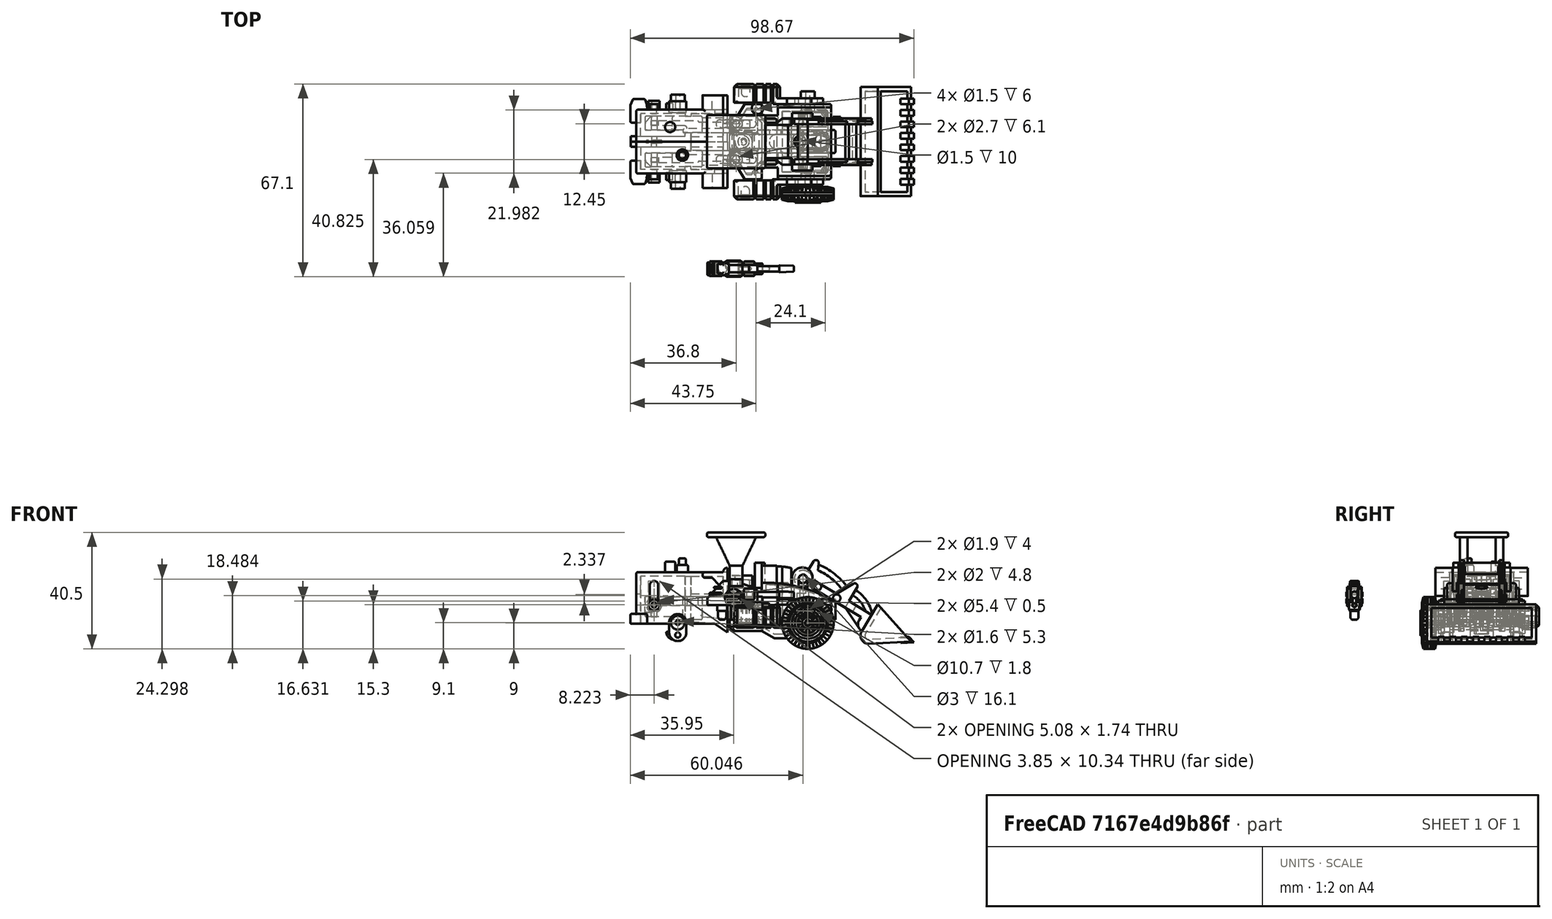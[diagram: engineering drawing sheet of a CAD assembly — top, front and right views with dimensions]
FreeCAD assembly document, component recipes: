
FREECAD ASSEMBLY — COMPONENT RECIPES ("Scrapper")

This assembly document has 14 components, labeled P0..P13 below (a component is one placed body or linked part). 14 of them carry a construction recipe — the FreeCAD feature program that regenerates the part from scratch, quoted from this document or its linked companion documents; the rest are supplied as boundary geometry only. No exploded tour is included for this assembly.
NOTE — document 2 of 4 of this assembly tour. The two overview renders and the header above are repeated from document 1; the component sections below continue where the previous document stopped.
COMPONENT P3 — recipe-attached ("Scoop", modeled in this document).
Construction recipe (the document's own serialized feature program — sketch geometry with constraints, then the solid features built on it; lengths are millimeters unless a unit is written):

FEATURE [Sketcher::SketchObject] Sketch111
  ArcFitTolerance = 1e-06
  AttachmentSupport = -> [XY_Plane004]
  FullyConstrained = true
  MakeInternals = false
  MapMode = 5
  sketch-geometry (4):
    g0: LineSegment StartX=3.75398 StartY=13.5 StartZ=0 EndX=14.5725 EndY=0 EndZ=0
    g1: LineSegment StartX=3.75398 StartY=13.5 StartZ=0 EndX=-2.36 EndY=4.43565 EndZ=0
    g2: ArcOfCircle CenterX=0 CenterY=2.84565 CenterZ=0 NormalX=0 NormalY=0 NormalZ=1 AngleXU=0 Radius=2.84565 StartAngle=2.54872 EndAngle=4.71239
    g3: LineSegment StartX=-5e-16 StartY=0 StartZ=0 EndX=14.5725 EndY=0 EndZ=0
  constraints (12):
    c: PointOnObject(g0,g-1)
    c: Coincident(g1,g0)
    c: Coincident(g2,g1)
    c: Distance(g0) = 17.3
    c: Coincident(g3,g2)
    c: Coincident(g3,g0)
    c: DistanceY(g2,g0) = 13.5
    c: Coincident(g2,g-1)
    c: Angle(g3,g1) = 0.977384
    c: DistanceX(g2,g2) = 0
    c: DistanceX(g1,g2) = 2.36
    c: DistanceY(g2,g1) = 1.59
FEATURE [PartDesign::Pad] Pad065
  Direction = (0,0,1)
  Length = 38
  Length2 = 10
  Profile = -> Sketch111
  ReferenceAxis = -> Sketch111 [N_Axis]
  Refine = true
  Suppressed = false
  Type = 0
FEATURE [Sketcher::SketchObject] Sketch112
  ArcFitTolerance = 1e-06
  AttachmentSupport = -> [Pad065]
  ExternalGeometry = -> [Pad065]
  FullyConstrained = false
  MakeInternals = false
  MapMode = 5
  Placement = pos=(0,0,38) rot=(0,0,1;0rad)
  sketch-geometry (6):
    g0: LineSegment StartX=4.73641 StartY=12.2741 StartZ=0 EndX=-1.11618 EndY=3.59725 EndZ=0
    g1: ArcOfCircle CenterX=0 CenterY=2.84565 CenterZ=0 NormalX=0 NormalY=0 NormalZ=1 AngleXU=0 Radius=1.34565 StartAngle=2.54896 EndAngle=4.71239
    g2: LineSegment StartX=0 StartY=1.5 StartZ=0 EndX=13.3704 EndY=1.5 EndZ=0
    g3: LineSegment [constr] StartX=1.25379 StartY=9.79331 StartZ=0 EndX=2.49735 EndY=8.95452 EndZ=0
    g4: LineSegment [constr] StartX=6.46619 StartY=7.71687 StartZ=0 EndX=7.63671 EndY=8.65489 EndZ=0
    g5: LineSegment StartX=4.73641 StartY=12.2741 StartZ=0 EndX=13.3704 EndY=1.5 EndZ=0
  constraints (19):
    c: Coincident(g1,g0)
    c: PointOnObject(g1,g-2)
    c: Coincident(g2,g1)
    c: Horizontal(g2)
    c: Parallel(g0,g-4)
    c: DistanceY(g-6,g2) = 1.5
    c: Diameter(g-5) = 5.69129
    c: Coincident(g1,g-5)
    c: PointOnObject(g3,g-4)
    c: PointOnObject(g3,g0)
    c: Angle(g-4,g3) = 1.5708
    c: Distance(g3) = 1.5
    c: PointOnObject(g4,g-3)
    c: Angle(g4,g-3) = 1.5708
    c: Distance(g4) = 1.5
    c: PointOnObject(g0,g-3)
    c: PointOnObject(g2,g-3)
    c: Coincident(g5,g0)
    c: Coincident(g5,g2)
FEATURE [PartDesign::Pocket] Pocket058
  BaseFeature = -> Pad065
  Direction = (0,0,-1)
  Length = 36.5
  Length2 = 5
  Profile = -> Sketch112
  ReferenceAxis = -> Sketch112 [N_Axis]
  Refine = true
  Suppressed = false
  Type = 0
FEATURE [Sketcher::SketchObject] Sketch113
  ArcFitTolerance = 1e-06
  AttachmentSupport = -> [Pocket058]
  ExternalGeometry = -> [Pocket058]
  FullyConstrained = true
  MakeInternals = false
  MapMode = 5
  Placement = pos=(0,0,38) rot=(0,0,1;0rad)
  sketch-geometry (4):
    g0: LineSegment StartX=4.73641 StartY=12.2741 StartZ=0 EndX=13.3704 EndY=1.5 EndZ=0
    g1: LineSegment StartX=13.3704 StartY=1.5 StartZ=0 EndX=0 EndY=1.5 EndZ=0
    g2: LineSegment StartX=4.73641 StartY=12.2741 StartZ=0 EndX=-1.11618 EndY=3.59725 EndZ=0
    g3: ArcOfCircle CenterX=8.7599e-06 CenterY=2.84565 CenterZ=0 NormalX=0 NormalY=0 NormalZ=1 AngleXU=0 Radius=1.34565 StartAngle=2.54897 EndAngle=4.71238
  constraints (9):
    c: Coincident(g0,g-3)
    c: Coincident(g0,g-5)
    c: Coincident(g2,g0)
    c: Coincident(g2,g-4)
    c: Coincident(g3,g1)
    c: Coincident(g3,g2)
    c: Coincident(g1,g-5)
    c: Tangent(g3,g-4)
    c: Coincident(g1,g0)
FEATURE [PartDesign::Pad] Pad066
  BaseFeature = -> Pocket058
  Direction = (0,0,1)
  Length = 1.5
  Length2 = 10
  Profile = -> Sketch113
  ReferenceAxis = -> Sketch113 [N_Axis]
  Refine = true
  Reversed = true
  Suppressed = false
  Type = 0
FEATURE [Sketcher::SketchObject] Sketch114
  ArcFitTolerance = 1e-06
  AttachmentSupport = -> [Pad066]
  ExternalGeometry = -> [Pad066]
  FullyConstrained = true
  MakeInternals = false
  MapMode = 5
  Placement = pos=(0,0,0) rot=(1,0,0;1.5708rad)
  sketch-geometry (32):
    g0: LineSegment StartX=10.9725 StartY=34 StartZ=0 EndX=10.9725 EndY=32 EndZ=0
    g1: LineSegment StartX=10.9725 StartY=32 StartZ=0 EndX=15.5725 EndY=32 EndZ=0
    g2: LineSegment StartX=15.5725 StartY=32 StartZ=0 EndX=15.5725 EndY=34 EndZ=0
    g3: LineSegment StartX=15.5725 StartY=34 StartZ=0 EndX=10.9725 EndY=34 EndZ=0
    g4: LineSegment StartX=10.9725 StartY=30 StartZ=0 EndX=10.9725 EndY=28 EndZ=0
    g5: LineSegment StartX=10.9725 StartY=28 StartZ=0 EndX=15.5725 EndY=28 EndZ=0
    g6: LineSegment StartX=15.5725 StartY=28 StartZ=0 EndX=15.5725 EndY=30 EndZ=0
    g7: LineSegment StartX=15.5725 StartY=30 StartZ=0 EndX=10.9725 EndY=30 EndZ=0
    g8: LineSegment StartX=10.9725 StartY=26 StartZ=0 EndX=10.9725 EndY=24 EndZ=0
    g9: LineSegment StartX=10.9725 StartY=24 StartZ=0 EndX=15.5725 EndY=24 EndZ=0
    g10: LineSegment StartX=15.5725 StartY=24 StartZ=0 EndX=15.5725 EndY=26 EndZ=0
    g11: LineSegment StartX=15.5725 StartY=26 StartZ=0 EndX=10.9725 EndY=26 EndZ=0
    g12: LineSegment StartX=10.9725 StartY=22 StartZ=0 EndX=10.9725 EndY=20 EndZ=0
    g13: LineSegment StartX=10.9725 StartY=20 StartZ=0 EndX=15.5725 EndY=20 EndZ=0
    g14: LineSegment StartX=15.5725 StartY=20 StartZ=0 EndX=15.5725 EndY=22 EndZ=0
    g15: LineSegment StartX=15.5725 StartY=22 StartZ=0 EndX=10.9725 EndY=22 EndZ=0
    g16: LineSegment StartX=10.9725 StartY=18 StartZ=0 EndX=10.9725 EndY=16 EndZ=0
    g17: LineSegment StartX=10.9725 StartY=16 StartZ=0 EndX=15.5725 EndY=16 EndZ=0
    g18: LineSegment StartX=15.5725 StartY=16 StartZ=0 EndX=15.5725 EndY=18 EndZ=0
    g19: LineSegment StartX=15.5725 StartY=18 StartZ=0 EndX=10.9725 EndY=18 EndZ=0
    g20: LineSegment StartX=10.9725 StartY=14 StartZ=0 EndX=10.9725 EndY=12 EndZ=0
    g21: LineSegment StartX=10.9725 StartY=12 StartZ=0 EndX=15.5725 EndY=12 EndZ=0
    g22: LineSegment StartX=15.5725 StartY=12 StartZ=0 EndX=15.5725 EndY=14 EndZ=0
    g23: LineSegment StartX=15.5725 StartY=14 StartZ=0 EndX=10.9725 EndY=14 EndZ=0
    g24: LineSegment StartX=10.9725 StartY=10 StartZ=0 EndX=10.9725 EndY=8 EndZ=0
    g25: LineSegment StartX=10.9725 StartY=8 StartZ=0 EndX=15.5725 EndY=8 EndZ=0
    g26: LineSegment StartX=15.5725 StartY=8 StartZ=0 EndX=15.5725 EndY=10 EndZ=0
    g27: LineSegment StartX=15.5725 StartY=10 StartZ=0 EndX=10.9725 EndY=10 EndZ=0
    g28: LineSegment StartX=10.9725 StartY=6 StartZ=0 EndX=10.9725 EndY=4 EndZ=0
    g29: LineSegment StartX=10.9725 StartY=4 StartZ=0 EndX=15.5725 EndY=4 EndZ=0
    g30: LineSegment StartX=15.5725 StartY=4 StartZ=0 EndX=15.5725 EndY=6 EndZ=0
    g31: LineSegment StartX=15.5725 StartY=6 StartZ=0 EndX=10.9725 EndY=6 EndZ=0
  constraints (97):
    c: Coincident(g0,g1)
    c: Coincident(g1,g2)
    c: Coincident(g2,g3)
    c: Coincident(g3,g0)
    c: Vertical(g0)
    c: Vertical(g2)
    c: Horizontal(g1)
    c: Horizontal(g3)
    c: Coincident(g4,g5)
    c: Coincident(g5,g6)
    c: Coincident(g6,g7)
    c: Coincident(g7,g4)
    c: Vertical(g4)
    c: Vertical(g6)
    c: Horizontal(g5)
    c: Horizontal(g7)
    c: Coincident(g8,g9)
    c: Coincident(g9,g10)
    c: Coincident(g10,g11)
    c: Coincident(g11,g8)
    c: Vertical(g8)
    c: Vertical(g10)
    c: Horizontal(g9)
    c: Horizontal(g11)
    c: Coincident(g12,g13)
    c: Coincident(g13,g14)
    c: Coincident(g14,g15)
    c: Coincident(g15,g12)
    c: Vertical(g12)
    c: Vertical(g14)
    c: Horizontal(g13)
    c: Horizontal(g15)
    c: Coincident(g16,g17)
    c: Coincident(g17,g18)
    c: Coincident(g18,g19)
    c: Coincident(g19,g16)
    c: Vertical(g16)
    c: Vertical(g18)
    c: Horizontal(g17)
    c: Horizontal(g19)
    c: Coincident(g20,g21)
    c: Coincident(g21,g22)
    c: Coincident(g22,g23)
    c: Coincident(g23,g20)
    c: Vertical(g20)
    c: Vertical(g22)
    c: Horizontal(g21)
    c: Horizontal(g23)
    c: Coincident(g24,g25)
    c: Coincident(g25,g26)
    c: Coincident(g26,g27)
    c: Coincident(g27,g24)
    c: Vertical(g24)
    c: Vertical(g26)
    c: Horizontal(g25)
    c: Horizontal(g27)
    c: Coincident(g28,g29)
    c: Coincident(g29,g30)
    c: Coincident(g30,g31)
    c: Coincident(g31,g28)
    c: Vertical(g28)
    c: Vertical(g30)
    c: Horizontal(g29)
    c: Horizontal(g31)
    c: DistanceY(g30,g30) = 2
    c: DistanceY(g26,g26) = 2
    c: DistanceY(g22,g22) = 2
    c: DistanceY(g18,g18) = 2
    c: DistanceY(g14,g14) = 2
    c: DistanceY(g10,g10) = 2
    c: DistanceY(g6,g6) = 2
    c: DistanceY(g2,g2) = 2
    c: DistanceY(g4,g0) = 2
    c: DistanceY(g8,g4) = 2
    c: DistanceY(g12,g8) = 2
    c: DistanceY(g16,g12) = 2
    c: DistanceY(g20,g16) = 2
    c: DistanceX(g20,g16) = 0
    c: DistanceX(g16,g12) = 0
    c: DistanceX(g12,g8) = 0
    c: DistanceX(g4,g8) = 0
    c: DistanceX(g4,g0) = 0
    c: DistanceX(g3,g3) = 4.6
    c: DistanceX(g7,g7) = 4.6
    c: DistanceX(g11,g11) = 4.6
    c: DistanceX(g15,g15) = 4.6
    c: DistanceX(g19,g19) = 4.6
    c: DistanceX(g23,g23) = 4.6
    c: DistanceX(g27,g27) = 4.6
    c: DistanceX(g31,g31) = 4.6
    c: DistanceX(g20,g24) = 0
    c: DistanceX(g24,g28) = 0
    c: DistanceY(g24,g20) = 2
    c: DistanceY(g28,g24) = 2
    c: DistanceX(g-3,g2) = 1
    c: DistanceY(g2,g-3) = 4
    c: DistanceY(g-3,g29) = 4
FEATURE [PartDesign::Pad] Pad067
  BaseFeature = -> Pad066
  Direction = (0,-1,2e-16)
  Length = 0.25
  Length2 = 10
  Profile = -> Sketch114
  ReferenceAxis = -> Sketch114 [N_Axis]
  Refine = true
  Suppressed = false
  Type = 0
FEATURE [PartDesign::Pad] Pad068
  BaseFeature = -> Pad067
  Direction = (0,-1,2e-16)
  Length = 1.75
  Length2 = 10
  Profile = -> Sketch114
  ReferenceAxis = -> Sketch114 [N_Axis]
  Refine = true
  Reversed = true
  Suppressed = false
  Type = 0
FEATURE [Sketcher::SketchObject] Sketch115
  ArcFitTolerance = 1e-06
  AttachmentSupport = -> [Pad068]
  ExternalGeometry = -> [Pad068]
  FullyConstrained = true
  MakeInternals = false
  MapMode = 5
  Placement = pos=(0,0,34) rot=(0,0,1;0rad)
  sketch-geometry (3):
    g0: LineSegment StartX=15.5725 StartY=1.75 StartZ=0 EndX=15.5725 EndY=-0.25 EndZ=0
    g1: LineSegment StartX=15.5725 StartY=1.75 StartZ=0 EndX=13.9697 EndY=1.75 EndZ=0
    g2: LineSegment StartX=13.9697 StartY=1.75 StartZ=0 EndX=15.5725 EndY=-0.25 EndZ=0
  constraints (7):
    c: Coincident(g0,g-4)
    c: Coincident(g0,g-3)
    c: Coincident(g1,g0)
    c: PointOnObject(g1,g-4)
    c: Coincident(g2,g1)
    c: Coincident(g2,g0)
    c: Parallel(g-5,g2)
FEATURE [PartDesign::Pocket] Pocket059
  BaseFeature = -> Pad068
  Direction = (0,0,-1)
  Length = 30
  Length2 = 5
  Profile = -> Sketch115
  ReferenceAxis = -> Sketch115 [N_Axis]
  Refine = true
  Suppressed = false
  Type = 0
FEATURE [Sketcher::SketchObject] Sketch116
  ArcFitTolerance = 1e-06
  AttachmentOffset = pos=(0,0,-10.9) rot=(0,0,1;0rad)
  AttachmentSupport = -> [Pocket059]
  ExternalGeometry = -> [Pocket059]
  FullyConstrained = true
  MakeInternals = false
  MapMode = 5
  Placement = pos=(0,0,27.1) rot=(0,0,1;0rad)
  sketch-geometry (28):
    g0: LineSegment [constr] StartX=1.40537 StartY=10.018 StartZ=0 EndX=-2.2853 EndY=4.54639 EndZ=0
    g1: LineSegment StartX=1.40537 StartY=10.018 StartZ=0 EndX=-2.2853 EndY=4.54639 EndZ=0
    g2: LineSegment StartX=1.40537 StartY=10.018 StartZ=0 EndX=-6.22177 EndY=15.1626 EndZ=0
    g3: LineSegment StartX=-2.36983 StartY=9.42828 StartZ=0 EndX=-20.0283 EndY=21.3391 EndZ=0
    g4: LineSegment [constr] StartX=-2.90562 StartY=12.9258 StartZ=0 EndX=-4.35952 EndY=10.7703 EndZ=0
    g5: LineSegment StartX=-2.36983 StartY=9.42828 StartZ=0 EndX=-3.04086 EndY=8.43344 EndZ=0
    g6: LineSegment [constr] StartX=-2.36983 StartY=9.42828 StartZ=0 EndX=-0.0485276 EndY=7.86254 EndZ=0
    g7: ArcOfCircle CenterX=-0.719559 CenterY=6.8677 CenterZ=0 NormalX=0 NormalY=0 NormalZ=1 AngleXU=0 Radius=2.8 StartAngle=2.54818 EndAngle=4.11898
    g8: LineSegment [constr] StartX=-3.04086 StartY=8.43344 StartZ=0 EndX=-0.719559 EndY=6.8677 EndZ=0
    g9: ArcOfCircle CenterX=-21.8495 CenterY=23.7231 CenterZ=0 NormalX=0 NormalY=0 NormalZ=1 AngleXU=0 Radius=3 StartAngle=0.977384 EndAngle=5.36474
    g10: LineSegment StartX=-6.22177 StartY=15.1626 StartZ=0 EndX=-3.14621 EndY=19.7223 EndZ=0
    g11: ArcOfCircle CenterX=-3.97525 CenterY=20.2815 CenterZ=0 NormalX=0 NormalY=0 NormalZ=1 AngleXU=0 Radius=1 StartAngle=5.68977 EndAngle=8.35015
    g12: LineSegment StartX=-4.45131 StartY=21.1609 StartZ=0 EndX=-10.367 EndY=17.9586 EndZ=0
    g13: LineSegment StartX=-10.367 StartY=17.9586 StartZ=0 EndX=-17.0822 EndY=22.488 EndZ=0
    g14: LineSegment StartX=-17.0822 StartY=22.488 StartZ=0 EndX=-16.033 EndY=28.9729 EndZ=0
    g15: ArcOfCircle CenterX=-17.0267 CenterY=29.0848 CenterZ=0 NormalX=0 NormalY=0 NormalZ=1 AngleXU=0 Radius=1 StartAngle=6.17099 EndAngle=8.83137
    g16: LineSegment StartX=-17.8558 StartY=29.644 StartZ=0 EndX=-20.1719 EndY=26.2102 EndZ=0
    g17: LineSegment [constr] StartX=-13.7246 StartY=20.2233 StartZ=0 EndX=-15.1785 EndY=18.0678 EndZ=0
    g18: LineSegment [constr] StartX=-3.14621 StartY=19.7223 StartZ=0 EndX=-3.97525 EndY=20.2815 EndZ=0
    g19: LineSegment [constr] StartX=-3.97525 StartY=20.2815 StartZ=0 EndX=-4.45131 EndY=21.1609 EndZ=0
    g20: LineSegment [constr] StartX=-6.22177 StartY=15.1626 StartZ=0 EndX=-10.367 EndY=17.9586 EndZ=0
    g21: LineSegment [constr] StartX=-3.97525 StartY=20.2815 StartZ=0 EndX=-7.05081 EndY=15.7218 EndZ=0
    g22: LineSegment [constr] StartX=-3.97525 StartY=20.2815 StartZ=0 EndX=-17.0267 EndY=29.0848 EndZ=0
    g23: LineSegment [constr] StartX=-17.0267 StartY=29.0848 StartZ=0 EndX=-17.8558 EndY=29.644 EndZ=0
    g24: LineSegment [constr] StartX=-17.0267 StartY=29.0848 StartZ=0 EndX=-16.033 EndY=28.9729 EndZ=0
    g25: LineSegment [constr] StartX=-20.1719 StartY=26.2102 StartZ=0 EndX=-21.8495 EndY=23.7231 EndZ=0
    g26: LineSegment [constr] StartX=-20.0283 StartY=21.3391 StartZ=0 EndX=-24.9197 EndY=24.6383 EndZ=0
    g27: LineSegment [constr] StartX=-24.9197 StartY=24.6383 StartZ=0 EndX=-22.1237 EndY=28.7835 EndZ=0
  constraints (82):
    c: PointOnObject(g0,g-3)
    c: Distance(g-3,g0) = 4.2
    c: Distance(g0) = 6.6
    c: PointOnObject(g-4,g0)
    c: Coincident(g1,g0)
    c: Coincident(g1,g0)
    c: Coincident(g2,g0)
    c: PointOnObject(g4,g2)
    c: PointOnObject(g4,g3)
    c: Angle(g4,g2) = 1.5708
    c: Angle(g3,g4) = 1.5708
    c: Distance(g4) = 2.6
    c: Angle(g2,g1) = 1.5708
    c: Coincident(g5,g3)
    c: Angle(g3,g5) = 1.5708
    c: Coincident(g6,g3)
    c: PointOnObject(g6,g1)
    c: Angle(g5,g6) = 1.5708
    c: Distance(g6) = 2.8
    c: Coincident(g7,g0)
    c: Coincident(g7,g5)
    c: Coincident(g8,g5)
    c: PointOnObject(g8,g1)
    c: Angle(g8,g5) = 1.5708
    c: Coincident(g7,g8)
    c: Distance(g2) = 9.2
    c: Distance(g3) = 21.3
    c: Coincident(g9,g3)
    c: Radius(g9) = 3
    c: Coincident(g10,g2)
    c: Coincident(g11,g10)
    c: Coincident(g12,g11)
    c: Coincident(g13,g12)
    c: Coincident(g14,g13)
    c: Coincident(g15,g14)
    c: Coincident(g16,g15)
    c: Coincident(g9,g16)
    c: Parallel(g13,g3)
    c: Angle(g2,g10) = 1.5708
    c: Symmetric(g13,g13,g17)
    c: PointOnObject(g17,g3)
    c: Angle(g17,g13) = 1.5708
    c: Distance(g4,g2) = 4
    c: Distance(g17) = 2.6
    c: Distance(g2,g12) = 5
    c: Diameter(g11) = 2
    c: Diameter(g15) = 2
    c: Parallel(g16,g10)
    c: Coincident(g18,g10)
    c: Coincident(g18,g11)
    c: Angle(g18,g10) = 1.5708
    c: Coincident(g19,g11)
    c: Coincident(g19,g11)
    c: Angle(g12,g19) = 1.5708
    c: Coincident(g20,g2)
    c: Coincident(g20,g12)
    c: Coincident(g21,g11)
    c: PointOnObject(g21,g20)
    c: Angle(g21,g20) = 1.5708
    c: Distance(g21) = 5.5
    c: Distance(g13) = 8.1
    c: Coincident(g22,g11)
    c: Coincident(g22,g15)
    c: Parallel(g22,g13)
    c: Coincident(g23,g15)
    c: Coincident(g23,g15)
    c: Angle(g23,g22) = 3.14159
    c: Coincident(g24,g15)
    c: Coincident(g24,g14)
    c: Angle(g19,g22) = 0.481218  'Angle1'
    c: Angle(g22,g24) = 0.481219
    c: Angle(g12,g13) = 2.05201
    c: Coincident(g25,g9)
    c: Coincident(g25,g9)
    c: Angle(g16,g25) = 3.14159
    c: Coincident(g26,g3)
    c: Angle(g3,g26) = 3.14159
    c: Distance(g6,g26) = 30
    c: Coincident(g27,g26)
    c: Angle(g26,g27) = 1.5708
    c: Distance(g27) = 5
    c: Angle(g13,g14) = 2.00381
FEATURE [PartDesign::Pad] Pad069
  BaseFeature = -> Pocket059
  Direction = (0,0,1)
  Length = 16.2
  Length2 = 10
  Profile = -> Sketch116
  ReferenceAxis = -> Sketch116 [N_Axis]
  Refine = true
  Reversed = true
  Suppressed = false
  Type = 0
FEATURE [Sketcher::SketchObject] Sketch117
  ArcFitTolerance = 1e-06
  AttachmentOffset = pos=(0,0,7) rot=(0,0,1;0rad)
  AttachmentSupport = -> [Pad069]
  ExternalGeometry = -> [Pad069]
  FullyConstrained = true
  MakeInternals = false
  MapMode = 5
  Placement = pos=(-0.284513,-0.421807,-1.2e-15) rot=(0.917878,-0.280624,-0.280624;1.65638rad)
  sketch-geometry (4):
    g0: LineSegment StartX=-34.3798 StartY=25.1 StartZ=0 EndX=-34.3798 EndY=12.9 EndZ=0
    g1: LineSegment StartX=-34.3798 StartY=12.9 StartZ=0 EndX=-4.43691 EndY=12.9 EndZ=0
    g2: LineSegment StartX=-4.43691 StartY=12.9 StartZ=0 EndX=-4.43691 EndY=25.1 EndZ=0
    g3: LineSegment StartX=-4.43691 StartY=25.1 StartZ=0 EndX=-34.3798 EndY=25.1 EndZ=0
  constraints (12):
    c: Coincident(g0,g1)
    c: Coincident(g1,g2)
    c: Coincident(g2,g3)
    c: Coincident(g3,g0)
    c: Vertical(g0)
    c: Vertical(g2)
    c: Horizontal(g1)
    c: Horizontal(g3)
    c: PointOnObject(g2,g-3)
    c: DistanceY(g2,g-6) = 2
    c: DistanceY(g-7,g1) = 2
    c: DistanceX(g0,g-4) = 0
FEATURE [PartDesign::Pocket] Pocket060
  BaseFeature = -> Pad069
  Direction = (0.559193,0.829038,2e-16)
  Length = 17
  Length2 = 5
  Profile = -> Sketch117
  ReferenceAxis = -> Sketch117 [N_Axis]
  Refine = true
  Suppressed = false
  Type = 0
FEATURE [Sketcher::SketchObject] Sketch118
  ArcFitTolerance = 1e-06
  AttachmentSupport = -> [Pocket060]
  ExternalGeometry = -> [Pocket060]
  FullyConstrained = true
  MakeInternals = false
  MapMode = 5
  Placement = pos=(0,0,10.9) rot=(1,0,0;3.14159rad)
  sketch-geometry (3):
    g0: Circle CenterX=-10.4408 CenterY=-16.4403 CenterZ=0 NormalX=0 NormalY=0 NormalZ=1 AngleXU=0 Radius=1.3
    g1: Circle CenterX=-16.9073 CenterY=-20.802 CenterZ=0 NormalX=0 NormalY=0 NormalZ=1 AngleXU=0 Radius=1.3
    g2: LineSegment [constr] StartX=-10.367 StartY=-17.9586 StartZ=0 EndX=-12.9464 EndY=-16.5623 EndZ=0
  constraints (9):
    c: Diameter(g0) = 2.6
    c: Diameter(g1) = 2.6
    c: Tangent(g0,g-3)
    c: Tangent(g1,g-3)
    c: Coincident(g2,g-4)
    c: PointOnObject(g2,g-3)
    c: Angle(g-6,g2) = 3.14159
    c: Tangent(g2,g0)
    c: Distance(g0,g1) = 7.8
FEATURE [PartDesign::Pad] Pad070
  BaseFeature = -> Pocket060
  Direction = (0,0,-1)
  Length = 0.5
  Length2 = 10
  Profile = -> Sketch118
  ReferenceAxis = -> Sketch118 [N_Axis]
  Refine = true
  Suppressed = false
  Type = 0
FEATURE [PartDesign::Pad] Pad071
  BaseFeature = -> Pad070
  Direction = (0,0,-1)
  Length = 16.7
  Length2 = 10
  Profile = -> Sketch118
  ReferenceAxis = -> Sketch118 [N_Axis]
  Refine = true
  Reversed = true
  Suppressed = false
  Type = 0
FEATURE [Sketcher::SketchObject] Sketch119
  ArcFitTolerance = 1e-06
  AttachmentSupport = -> [Pad071]
  ExternalGeometry = -> [Pad071]
  FullyConstrained = true
  MakeInternals = false
  MapMode = 5
  Placement = pos=(5.08374,7.53695,2.2e-15) rot=(0.211303,0.691141,0.691141;2.72511rad)
  sketch-geometry (4):
    g0: LineSegment StartX=29.4934 StartY=25.1 StartZ=0 EndX=13.6369 EndY=25.1 EndZ=0
    g1: LineSegment StartX=13.6369 StartY=25.1 StartZ=0 EndX=13.6369 EndY=12.9 EndZ=0
    g2: LineSegment StartX=13.6369 StartY=12.9 StartZ=0 EndX=29.4934 EndY=12.9 EndZ=0
    g3: LineSegment StartX=29.4934 StartY=12.9 StartZ=0 EndX=29.4934 EndY=25.1 EndZ=0
  constraints (10):
    c: Coincident(g0,g1)
    c: Coincident(g1,g2)
    c: Coincident(g2,g3)
    c: Coincident(g3,g0)
    c: Horizontal(g2)
    c: Vertical(g1)
    c: Vertical(g3)
    c: PointOnObject(g-4,g2)
    c: Coincident(g0,g-5)
    c: Coincident(g0,g-6)
FEATURE [PartDesign::Pocket] Pocket061
  BaseFeature = -> Pad071
  Direction = (-0.559193,-0.829038,0)
  Length = 5
  Length2 = 5
  Profile = -> Sketch119
  ReferenceAxis = -> Sketch119 [N_Axis]
  Refine = true
  Suppressed = false
  Type = 0
FEATURE [Sketcher::SketchObject] Sketch120
  ArcFitTolerance = 1e-06
  AttachmentSupport = -> [Pocket061]
  ExternalGeometry = -> [Pocket061]
  FullyConstrained = true
  MakeInternals = false
  MapMode = 5
  Placement = pos=(0,0,10.9) rot=(1,0,0;3.14159rad)
  sketch-geometry (1):
    g0: Circle CenterX=-21.8495 CenterY=-23.7231 CenterZ=0 NormalX=0 NormalY=0 NormalZ=1 AngleXU=0 Radius=1.475
  constraints (2):
    c: Coincident(g0,g-3)
    c: Diameter(g0) = 2.95
FEATURE [PartDesign::Pad] Pad072
  BaseFeature = -> Pocket061
  Direction = (0,0,-1)
  Length = 1.2
  Length2 = 10
  Profile = -> Sketch120
  ReferenceAxis = -> Sketch120 [N_Axis]
  Refine = true
  Suppressed = false
  Type = 0
FEATURE [Sketcher::SketchObject] Sketch121
  ArcFitTolerance = 1e-06
  AttachmentSupport = -> [Pad072]
  ExternalGeometry = -> [Pad072]
  FullyConstrained = true
  MakeInternals = false
  MapMode = 5
  Placement = pos=(0,0,27.1) rot=(0,0,1;0rad)
  sketch-geometry (1):
    g0: Circle CenterX=-21.8495 CenterY=23.7231 CenterZ=0 NormalX=0 NormalY=0 NormalZ=1 AngleXU=0 Radius=1.475
  constraints (2):
    c: Coincident(g0,g-3)
    c: Diameter(g0) = 2.95
FEATURE [PartDesign::Pad] Pad073
  BaseFeature = -> Pad072
  Direction = (0,0,1)
  Length = 1.2
  Length2 = 10
  Profile = -> Sketch121
  ReferenceAxis = -> Sketch121 [N_Axis]
  Refine = true
  Suppressed = false
  Type = 0
FEATURE [Sketcher::SketchObject] Sketch122
  ArcFitTolerance = 1e-06
  AttachmentOffset = pos=(0,0,2) rot=(0,0,1;0rad)
  AttachmentSupport = -> [Pad073]
  ExternalGeometry = -> [Pad073]
  FullyConstrained = true
  MakeInternals = false
  MapMode = 5
  Placement = pos=(-27.6731,18.6658,2e-16) rot=(-0.351924,0.661872,0.661872;3.81837rad)
  sketch-geometry (6):
    g0: LineSegment StartX=-5.97422 StartY=28.3 StartZ=0 EndX=-5.97422 EndY=27.3 EndZ=0
    g1: LineSegment StartX=-5.97422 StartY=27.3 StartZ=0 EndX=-7.44922 EndY=28.3 EndZ=0
    g2: LineSegment StartX=-5.97422 StartY=28.3 StartZ=0 EndX=-7.44922 EndY=28.3 EndZ=0
    g3: LineSegment StartX=-5.97422 StartY=9.7 StartZ=0 EndX=-5.97422 EndY=10.7 EndZ=0
    g4: LineSegment StartX=-5.97422 StartY=10.7 StartZ=0 EndX=-7.44922 EndY=9.7 EndZ=0
    g5: LineSegment StartX=-7.44922 StartY=9.7 StartZ=0 EndX=-5.97422 EndY=9.7 EndZ=0
  constraints (16):
    c: PointOnObject(g1,g-3)
    c: DistanceX(g-3,g-3) = 2.95
    c: DistanceX(g1,g-3) = 1.475
    c: Coincident(g0,g-3)
    c: Vertical(g0)
    c: Coincident(g1,g0)
    c: Coincident(g2,g0)
    c: Coincident(g2,g1)
    c: DistanceY(g0,g0) = 1
    c: Coincident(g3,g-5)
    c: Vertical(g3)
    c: Coincident(g4,g3)
    c: Symmetric(g-5,g-5,g4)
    c: Coincident(g5,g4)
    c: Coincident(g5,g3)
    c: DistanceY(g3,g3) = 1
FEATURE [PartDesign::Pocket] Pocket062
  BaseFeature = -> Pad073
  Direction = (0.829038,-0.559193,-1e-16)
  Length = 4
  Length2 = 5
  Profile = -> Sketch122
  ReferenceAxis = -> Sketch122 [N_Axis]
  Refine = true
  Suppressed = false
  Type = 0
FEATURE [Sketcher::SketchObject] Sketch123
  ArcFitTolerance = 1e-06
  AttachmentSupport = -> [Pocket062]
  ExternalGeometry = -> [Pocket062]
  FullyConstrained = true
  MakeInternals = false
  MapMode = 5
  Placement = pos=(0,-7.3e-15,25.1) rot=(1,0,0;3.14159rad)
  sketch-geometry (4):
    g0: LineSegment StartX=-5.18856 StartY=-11.3295 StartZ=0 EndX=-7.67567 EndY=-13.0071 EndZ=0
    g1: LineSegment StartX=-7.67567 StartY=-13.0071 StartZ=0 EndX=-6.22177 EndY=-15.1626 EndZ=0
    g2: LineSegment StartX=-5.18856 StartY=-11.3295 StartZ=0 EndX=-3.73466 EndY=-13.485 EndZ=0
    g3: LineSegment StartX=-3.73466 StartY=-13.485 StartZ=0 EndX=-6.22177 EndY=-15.1626 EndZ=0
  constraints (11):
    c: Coincident(g1,g0)
    c: Coincident(g2,g0)
    c: Coincident(g3,g2)
    c: Coincident(g3,g1)
    c: Distance(g3) = 3
    c: PointOnObject(g2,g-3)
    c: PointOnObject(g0,g-4)
    c: PointOnObject(g0,g-4)
    c: Distance(g0) = 3
    c: Coincident(g1,g-3)
    c: Angle(g3,g1) = 1.5708
FEATURE [PartDesign::Pad] Pad074
  BaseFeature = -> Pocket062
  Direction = (0,0,-1)
  Length = 12.2
  Length2 = 10
  Profile = -> Sketch123
  ReferenceAxis = -> Sketch123 [N_Axis]
  Refine = true
  Suppressed = false
  Type = 0
FEATURE [Sketcher::SketchObject] Sketch124
  ArcFitTolerance = 1e-06
  AttachmentSupport = -> [Pad074]
  ExternalGeometry = -> [Pad074]
  FullyConstrained = true
  MakeInternals = false
  MapMode = 5
  Placement = pos=(0,-7.3e-15,25.1) rot=(1,0,0;3.14159rad)
  sketch-geometry (1):
    g0: Circle CenterX=-21.8495 CenterY=-23.7231 CenterZ=0 NormalX=0 NormalY=0 NormalZ=1 AngleXU=0 Radius=1.75
  constraints (2):
    c: Coincident(g0,g-3)
    c: Diameter(g0) = 3.5
FEATURE [PartDesign::Pad] Pad075
  BaseFeature = -> Pad074
  Direction = (0,0,-1)
  Length = 12.2
  Length2 = 10
  Profile = -> Sketch124
  ReferenceAxis = -> Sketch124 [N_Axis]
  Refine = true
  Suppressed = false
  Type = 0
FEATURE [Sketcher::SketchObject] Sketch125
  ArcFitTolerance = 1e-06
  AttachmentSupport = -> [Pad075]
  ExternalGeometry = -> [Pad075]
  FullyConstrained = true
  MakeInternals = false
  MapMode = 5
  Placement = pos=(0,0,10.9) rot=(1,0,0;3.14159rad)
  sketch-geometry (5):
    g0: LineSegment StartX=-17.0822 StartY=-22.488 StartZ=0 EndX=-18.5744 EndY=-23.4946 EndZ=0
    g1: ArcOfCircle CenterX=-21.5738 CenterY=-23.5578 CenterZ=0 NormalX=0 NormalY=0 NormalZ=1 AngleXU=0 Radius=3 StartAngle=5.1986 EndAngle=6.30427
    g2: LineSegment StartX=-20.1719 StartY=-26.2102 StartZ=0 EndX=-17.8558 EndY=-29.644 EndZ=0
    g3: LineSegment StartX=-17.0822 StartY=-22.488 StartZ=0 EndX=-16.033 EndY=-28.9729 EndZ=0
    g4: ArcOfCircle CenterX=-17.0267 CenterY=-29.0848 CenterZ=0 NormalX=0 NormalY=0 NormalZ=1 AngleXU=0 Radius=1 StartAngle=3.735 EndAngle=6.39538
  constraints (15):
    c: Diameter(g-3) = 6
    c: Coincident(g0,g-6)
    c: Coincident(g1,g-4)
    c: Coincident(g1,g0)
    c: Diameter(g1) = 6
    c: Angle(g0,g-8) = 3.14159
    c: Distance(g-9) = 2.88775
    c: Distance(g0,g-8) = 2.88775
    c: Coincident(g2,g1)
    c: Coincident(g2,g-5)
    c: Coincident(g3,g0)
    c: Coincident(g3,g-6)
    c: Coincident(g4,g3)
    c: Coincident(g4,g2)
    c: Tangent(g4,g-5)
FEATURE [PartDesign::Pocket] Pocket063
  BaseFeature = -> Pad075
  Direction = (0,0,1)
  Length = 0.5
  Length2 = 5
  Profile = -> Sketch125
  ReferenceAxis = -> Sketch125 [N_Axis]
  Refine = true
  Suppressed = false
  Type = 0
FEATURE [Sketcher::SketchObject] Sketch126
  ArcFitTolerance = 1e-06
  AttachmentSupport = -> [Pocket063]
  ExternalGeometry = -> [Pocket063]
  FullyConstrained = true
  MakeInternals = false
  MapMode = 5
  Placement = pos=(0,0,11.4) rot=(1,0,0;3.14159rad)
  sketch-geometry (7):
    g0: LineSegment StartX=-4.82379 StartY=-17.2352 StartZ=0 EndX=-6.22177 EndY=-15.1626 EndZ=0
    g1: LineSegment StartX=-6.22177 StartY=-15.1626 StartZ=0 EndX=-0.66722 EndY=-11.416 EndZ=0
    g2: ArcOfCircle CenterX=-11.0382 CenterY=-8.40225 CenterZ=0 NormalX=0 NormalY=0 NormalZ=1 AngleXU=0 Radius=10.8 StartAngle=5.32549 EndAngle=6.00038
    g3: LineSegment StartX=-17.0822 StartY=-22.488 StartZ=0 EndX=-16.4433 EndY=-26.4367 EndZ=0
    g4: LineSegment StartX=-17.0822 StartY=-22.488 StartZ=0 EndX=-10.367 EndY=-17.9586 EndZ=0
    g5: ArcOfCircle CenterX=-25.5291 CenterY=-8.0601 CenterZ=0 NormalX=0 NormalY=0 NormalZ=1 AngleXU=0 Radius=20.5 StartAngle=5.17156 EndAngle=5.71443
    g6: LineSegment StartX=-10.367 StartY=-17.9586 StartZ=0 EndX=-8.25637 EndY=-19.1011 EndZ=0
  constraints (20):
    c: PointOnObject(g0,g-6)
    c: Coincident(g0,g-7)
    c: Coincident(g1,g0)
    c: PointOnObject(g1,g-7)
    c: Coincident(g2,g0)
    c: Coincident(g2,g1)
    c: Coincident(g3,g-3)
    c: PointOnObject(g3,g-3)
    c: Coincident(g4,g3)
    c: Coincident(g4,g-5)
    c: Coincident(g5,g3)
    c: PointOnObject(g5,g-5)
    c: Distance(g3) = 4
    c: Coincident(g6,g4)
    c: Coincident(g6,g5)
    c: Distance(g6) = 2.4
    c: Distance(g0) = 2.5
    c: Distance(g1) = 6.7
    c: Radius(g2) = 10.8
    c: Radius(g5) = 20.5
FEATURE [PartDesign::Pad] Pad076
  BaseFeature = -> Pocket063
  Direction = (0,0,-1)
  Length = 1.5
  Length2 = 10
  Profile = -> Sketch126
  ReferenceAxis = -> Sketch126 [N_Axis]
  Refine = true
  Reversed = true
  Suppressed = false
  Type = 0
FEATURE [Sketcher::SketchObject] Sketch127
  ArcFitTolerance = 1e-06
  AttachmentSupport = -> [Pad076]
  ExternalGeometry = -> [Pad076]
  FullyConstrained = true
  MakeInternals = false
  MapMode = 5
  Placement = pos=(0,0,27.1) rot=(0,0,1;0rad)
  sketch-geometry (5):
    g0: ArcOfCircle CenterX=-21.5738 CenterY=23.5578 CenterZ=0 NormalX=0 NormalY=0 NormalZ=1 AngleXU=0 Radius=3 StartAngle=6.2621 EndAngle=7.36777
    g1: LineSegment StartX=-17.0822 StartY=22.488 StartZ=0 EndX=-18.5744 EndY=23.4946 EndZ=0
    g2: LineSegment StartX=-17.0822 StartY=22.488 StartZ=0 EndX=-16.033 EndY=28.9729 EndZ=0
    g3: LineSegment StartX=-17.8558 StartY=29.644 StartZ=0 EndX=-20.1719 EndY=26.2102 EndZ=0
    g4: ArcOfCircle CenterX=-17.0267 CenterY=29.0848 CenterZ=0 NormalX=0 NormalY=0 NormalZ=1 AngleXU=0 Radius=1 StartAngle=6.17099 EndAngle=8.83137
  constraints (13):
    c: Coincident(g0,g-6)
    c: Coincident(g1,g-4)
    c: Coincident(g1,g0)
    c: Angle(g1,g-3) = 3.14159
    c: Radius(g0) = 3
    c: PointOnObject(g-7,g0)
    c: Coincident(g2,g-4)
    c: Coincident(g3,g-6)
    c: Coincident(g3,g0)
    c: Coincident(g4,g3)
    c: Coincident(g4,g2)
    c: Tangent(g4,g-8)
    c: Coincident(g2,g1)
FEATURE [PartDesign::Pocket] Pocket064
  BaseFeature = -> Pad076
  Direction = (0,0,-1)
  Length = 0.5
  Length2 = 5
  Profile = -> Sketch127
  ReferenceAxis = -> Sketch127 [N_Axis]
  Refine = true
  Suppressed = false
  Type = 0
FEATURE [Sketcher::SketchObject] Sketch128
  ArcFitTolerance = 1e-06
  AttachmentSupport = -> [Pocket064]
  ExternalGeometry = -> [Pocket064]
  FullyConstrained = true
  MakeInternals = false
  MapMode = 5
  Placement = pos=(0,0,26.6) rot=(0,0,1;0rad)
  sketch-geometry (7):
    g0: LineSegment StartX=-16.4433 StartY=26.4367 StartZ=0 EndX=-17.0822 EndY=22.488 EndZ=0
    g1: LineSegment StartX=-17.0822 StartY=22.488 StartZ=0 EndX=-10.367 EndY=17.9586 EndZ=0
    g2: LineSegment StartX=-10.367 StartY=17.9586 StartZ=0 EndX=-8.25637 EndY=19.1011 EndZ=0
    g3: ArcOfCircle CenterX=-25.5291 CenterY=8.06009 CenterZ=0 NormalX=0 NormalY=0 NormalZ=1 AngleXU=0 Radius=20.5 StartAngle=0.568759 EndAngle=1.11162
    g4: ArcOfCircle CenterX=-11.0382 CenterY=8.40225 CenterZ=0 NormalX=0 NormalY=0 NormalZ=1 AngleXU=0 Radius=10.8 StartAngle=0.282808 EndAngle=0.957693
    g5: LineSegment StartX=-4.82379 StartY=17.2352 StartZ=0 EndX=-6.22177 EndY=15.1626 EndZ=0
    g6: LineSegment StartX=-6.22177 StartY=15.1626 StartZ=0 EndX=-0.66722 EndY=11.416 EndZ=0
  constraints (15):
    c: Coincident(g0,g-6)
    c: Coincident(g0,g-3)
    c: Coincident(g1,g0)
    c: Coincident(g1,g-5)
    c: Coincident(g2,g1)
    c: Coincident(g2,g-6)
    c: Coincident(g3,g0)
    c: Coincident(g3,g2)
    c: Tangent(g3,g-6)
    c: Tangent(g4,g-9) = -1.5708
    c: Coincident(g4,g-9)
    c: Coincident(g5,g4)
    c: Coincident(g5,g-8)
    c: Coincident(g6,g5)
    c: Coincident(g6,g4)
FEATURE [PartDesign::Pad] Pad077
  BaseFeature = -> Pocket064
  Direction = (0,0,1)
  Length = 1.5
  Length2 = 10
  Profile = -> Sketch128
  ReferenceAxis = -> Sketch128 [N_Axis]
  Refine = true
  Reversed = true
  Suppressed = false
  Type = 0
FEATURE [Sketcher::SketchObject] Sketch129
  ArcFitTolerance = 1e-06
  AttachmentOffset = pos=(0,0,-0.5) rot=(0,0,1;0rad)
  AttachmentSupport = -> [Pad077]
  ExternalGeometry = -> [Pad077]
  FullyConstrained = true
  MakeInternals = false
  MapMode = 5
  Placement = pos=(-1.14e-14,9e-15,26.1) rot=(0,0,1;0rad)
  sketch-geometry (9):
    g0: LineSegment StartX=-16.4433 StartY=26.4367 StartZ=0 EndX=-16.1239 EndY=28.411 EndZ=0
    g1: LineSegment StartX=-8.25637 StartY=19.1011 StartZ=0 EndX=-6.56459 EndY=20.0169 EndZ=0
    g2: ArcOfCircle CenterX=-25.529 CenterY=8.06012 CenterZ=0 NormalX=0 NormalY=0 NormalZ=1 AngleXU=0 Radius=20.5 StartAngle=0.568758 EndAngle=1.11162
    g3: ArcOfCircle CenterX=-25.529 CenterY=8.06012 CenterZ=0 NormalX=0 NormalY=0 NormalZ=1 AngleXU=0 Radius=22.4191 StartAngle=0.562535 EndAngle=1.13789
    g4: LineSegment StartX=-0.66722 StartY=11.416 StartZ=0 EndX=1.40537 EndY=10.018 EndZ=0
    g5: LineSegment StartX=1.40537 StartY=10.018 StartZ=0 EndX=1.61553 EndY=10.3296 EndZ=0
    g6: ArcOfCircle CenterX=-11.0382 CenterY=8.40225 CenterZ=0 NormalX=0 NormalY=0 NormalZ=1 AngleXU=0 Radius=10.8 StartAngle=0.282808 EndAngle=0.957693
    g7: LineSegment StartX=-4.82379 StartY=17.2352 StartZ=0 EndX=-3.7054 EndY=18.8933 EndZ=0
    g8: ArcOfCircle CenterX=-11.0382 CenterY=8.40225 CenterZ=0 NormalX=0 NormalY=0 NormalZ=1 AngleXU=0 Radius=12.7997 StartAngle=0.151154 EndAngle=0.96077
  constraints (23):
    c: Coincident(g0,g-4)
    c: PointOnObject(g0,g-3)
    c: Coincident(g1,g-4)
    c: PointOnObject(g1,g-5)
    c: Coincident(g2,g0)
    c: Coincident(g2,g1)
    c: Tangent(g2,g-4)
    c: Coincident(g3,g0)
    c: Coincident(g3,g1)
    c: Distance(g0) = 2
    c: Coincident(g4,g-7)
    c: Coincident(g4,g-8)
    c: Coincident(g5,g4)
    c: PointOnObject(g5,g-9)
    c: Coincident(g6,g4)
    c: Tangent(g6,g-7) = -1.5708
    c: Coincident(g7,g6)
    c: PointOnObject(g7,g-6)
    c: Coincident(g8,g7)
    c: Coincident(g8,g5)
    c: Distance(g7) = 2
    c: Coincident(g6,g8)
    c: Coincident(g3,g2)
FEATURE [PartDesign::Pad] Pad078
  BaseFeature = -> Pad077
  Direction = (0,0,1)
  Length = 1
  Length2 = 10
  Profile = -> Sketch129
  ReferenceAxis = -> Sketch129 [N_Axis]
  Refine = true
  Reversed = true
  Suppressed = false
  Type = 0
FEATURE [Sketcher::SketchObject] Sketch130
  ArcFitTolerance = 1e-06
  AttachmentOffset = pos=(0,0,-0.5) rot=(0,0,1;0rad)
  AttachmentSupport = -> [Pad078]
  ExternalGeometry = -> [Pad078]
  FullyConstrained = true
  MakeInternals = false
  MapMode = 5
  Placement = pos=(0,0,11.9) rot=(1,0,0;3.14159rad)
  sketch-geometry (9):
    g0: LineSegment StartX=-0.66722 StartY=-11.416 StartZ=0 EndX=1.40537 EndY=-10.018 EndZ=0
    g1: LineSegment StartX=1.40537 StartY=-10.018 StartZ=0 EndX=1.61553 EndY=-10.3296 EndZ=0
    g2: LineSegment StartX=-4.82379 StartY=-17.2352 StartZ=0 EndX=-3.7054 EndY=-18.8933 EndZ=0
    g3: ArcOfCircle CenterX=-11.0382 CenterY=-8.40225 CenterZ=0 NormalX=0 NormalY=0 NormalZ=1 AngleXU=0 Radius=10.8 StartAngle=5.32549 EndAngle=6.00038
    g4: ArcOfCircle CenterX=-11.0382 CenterY=-8.40225 CenterZ=0 NormalX=0 NormalY=0 NormalZ=1 AngleXU=0 Radius=12.7997 StartAngle=5.32242 EndAngle=6.13203
    g5: ArcOfCircle CenterX=-25.5291 CenterY=-8.0601 CenterZ=0 NormalX=0 NormalY=0 NormalZ=1 AngleXU=0 Radius=20.5 StartAngle=5.17156 EndAngle=5.71443
    g6: ArcOfCircle CenterX=-25.529 CenterY=-8.06012 CenterZ=0 NormalX=0 NormalY=0 NormalZ=1 AngleXU=0 Radius=22.4191 StartAngle=5.1453 EndAngle=5.72065
    g7: LineSegment StartX=-8.25637 StartY=-19.1011 StartZ=0 EndX=-6.56459 EndY=-20.0169 EndZ=0
    g8: LineSegment StartX=-16.4433 StartY=-26.4367 StartZ=0 EndX=-16.1239 EndY=-28.411 EndZ=0
  constraints (20):
    c: Coincident(g0,g-3)
    c: Coincident(g0,g-4)
    c: Coincident(g1,g0)
    c: Coincident(g1,g-11)
    c: Coincident(g2,g-3)
    c: Coincident(g2,g-11)
    c: Coincident(g3,g2)
    c: Coincident(g3,g0)
    c: Tangent(g3,g-3)
    c: Coincident(g4,g1)
    c: Coincident(g4,g2)
    c: Tangent(g4,g-11)
    c: Tangent(g5,g-8) = -1.5708
    c: Coincident(g5,g-9)
    c: Tangent(g6,g-10) = -1.5708
    c: Coincident(g6,g-10)
    c: Coincident(g7,g5)
    c: Coincident(g7,g6)
    c: Coincident(g8,g5)
    c: Coincident(g8,g6)
FEATURE [PartDesign::Pad] Pad079
  BaseFeature = -> Pad078
  Direction = (0,0,-1)
  Length = 1
  Length2 = 10
  Profile = -> Sketch130
  ReferenceAxis = -> Sketch130 [N_Axis]
  Refine = true
  Reversed = true
  Suppressed = false
  Type = 0
FEATURE [Sketcher::SketchObject] Sketch131
  ArcFitTolerance = 1e-06
  AttachmentOffset = pos=(0,0,-0.5) rot=(0,0,1;0rad)
  AttachmentSupport = -> [Pad079]
  ExternalGeometry = -> [Pad079]
  FullyConstrained = true
  MakeInternals = false
  MapMode = 5
  Placement = pos=(0,0,11.4) rot=(1,0,0;3.14159rad)
  sketch-geometry (5):
    g0: LineSegment StartX=-3.04086 StartY=-8.43344 StartZ=0 EndX=-2.36983 EndY=-9.42828 EndZ=0
    g1: LineSegment StartX=-2.36983 StartY=-9.42828 StartZ=0 EndX=-7.67567 EndY=-13.0071 EndZ=0
    g2: ArcOfCircle CenterX=-0.719559 CenterY=-6.8677 CenterZ=0 NormalX=0 NormalY=0 NormalZ=1 AngleXU=0 Radius=2.8 StartAngle=2.65241 EndAngle=3.735
    g3: LineSegment StartX=-3.19117 StartY=-5.55197 StartZ=0 EndX=-7.67567 EndY=-13.0071 EndZ=0
    g4: LineSegment [constr] StartX=-6.22177 StartY=-15.1626 StartZ=0 EndX=-7.67567 EndY=-13.0071 EndZ=0
  constraints (12):
    c: Coincident(g0,g-4)
    c: Coincident(g0,g-5)
    c: Coincident(g1,g0)
    c: PointOnObject(g1,g-5)
    c: Coincident(g2,g0)
    c: Tangent(g2,g-3) = -1.5708
    c: Coincident(g3,g2)
    c: Coincident(g3,g1)
    c: Coincident(g4,g-6)
    c: Coincident(g4,g1)
    c: Angle(g4,g-6) = 3.14159
    c: Distance(g3) = 8.7
FEATURE [PartDesign::Pad] Pad080
  BaseFeature = -> Pad079
  Direction = (0,0,-1)
  Length = 1.5
  Length2 = 10
  Profile = -> Sketch131
  ReferenceAxis = -> Sketch131 [N_Axis]
  Refine = true
  Reversed = true
  Suppressed = false
  Type = 0
FEATURE [PartDesign::Body] Body004  label="Scoop"
  AllowCompound = false
  Group = -> [Sketch111,Pad065,Sketch112,Pocket058,Sketch113,Pad066,Sketch114,Pad067,Pad068,Sketch115,Pocket059,Sketch116,Pad069,Sketch117,Pocket060,Sketch118,Pad070,Pad071,Sketch119,Pocket061,Sketch120,Pad072,Sketch121,Pad073,Sketch122,Pocket062,Sketch123,Pad074,Sketch124,Pad075,Sketch125,Pocket063,Sketch126,Pad076,Sketch127,Pocket064,Sketch128,Pad077,Sketch129,Pad078,Sketch130,Pad079,Sketch131,Pad080,+10 more]
  Origin = -> Origin004
  Placement = pos=(13.2576,19,-13.4493) rot=(-0.999315,0.026168,-0.026168;4.7117rad)
  Tip = -> Pad198
COMPONENT P4 — recipe-attached ("Scoop_Stop", modeled in this document).
Construction recipe (the document's own serialized feature program — sketch geometry with constraints, then the solid features built on it; lengths are millimeters unless a unit is written):

FEATURE [Sketcher::SketchObject] Sketch251
  ArcFitTolerance = 1e-06
  AttachmentOffset = pos=(0,-0.05,0) rot=(0,0,1;0rad)
  AttachmentSupport = -> [XY_Plane008]
  FullyConstrained = true
  MakeInternals = false
  MapMode = 5
  Placement = pos=(0,-0.05,0) rot=(0,0,1;0rad)
  sketch-geometry (4):
    g0: LineSegment StartX=1.8e-15 StartY=0 StartZ=0 EndX=16 EndY=0 EndZ=0
    g1: LineSegment StartX=16 StartY=0 StartZ=0 EndX=16 EndY=5.2 EndZ=0
    g2: LineSegment StartX=16 StartY=5.2 StartZ=0 EndX=1.8e-15 EndY=5.2 EndZ=0
    g3: LineSegment StartX=1.8e-15 StartY=5.2 StartZ=0 EndX=1.8e-15 EndY=0 EndZ=0
  constraints (11):
    c: Coincident(g0,g1)
    c: Coincident(g1,g2)
    c: Coincident(g2,g3)
    c: Coincident(g3,g0)
    c: Horizontal(g0)
    c: Horizontal(g2)
    c: Vertical(g1)
    c: Vertical(g3)
    c: Coincident(g0,g-1)
    c: DistanceY(g1,g1) = 5.2
    c: DistanceX(g2,g2) = 16
FEATURE [PartDesign::Pad] Pad152
  Direction = (0,0,1)
  Length = 2
  Length2 = 10
  Profile = -> Sketch251
  ReferenceAxis = -> Sketch251 [N_Axis]
  Refine = true
  Suppressed = false
  Type = 0
FEATURE [Sketcher::SketchObject] Sketch252
  ArcFitTolerance = 1e-06
  AttachmentSupport = -> [Pad152]
  ExternalGeometry = -> [Pad152]
  FullyConstrained = true
  MakeInternals = false
  MapMode = 5
  Placement = pos=(0,0,0) rot=(1,0,0;3.14159rad)
  sketch-geometry (6):
    g0: LineSegment StartX=1.5 StartY=-5.15 StartZ=0 EndX=1.8e-15 EndY=-5.15 EndZ=0
    g1: LineSegment StartX=1.8e-15 StartY=-5.15 StartZ=0 EndX=1.8e-15 EndY=-3.25 EndZ=0
    g2: LineSegment StartX=1.8e-15 StartY=-3.25 StartZ=0 EndX=1.5 EndY=-5.15 EndZ=0
    g3: LineSegment StartX=16 StartY=-3.25 StartZ=0 EndX=16 EndY=-5.15 EndZ=0
    g4: LineSegment StartX=16 StartY=-5.15 StartZ=0 EndX=14.5 EndY=-5.15 EndZ=0
    g5: LineSegment StartX=14.5 StartY=-5.15 StartZ=0 EndX=16 EndY=-3.25 EndZ=0
  constraints (16):
    c: PointOnObject(g0,g-3)
    c: Coincident(g0,g-5)
    c: Coincident(g1,g0)
    c: PointOnObject(g1,g-5)
    c: Coincident(g2,g1)
    c: Coincident(g2,g0)
    c: PointOnObject(g3,g-4)
    c: Coincident(g3,g-4)
    c: Coincident(g4,g3)
    c: PointOnObject(g4,g-3)
    c: Coincident(g5,g4)
    c: Coincident(g5,g3)
    c: DistanceX(g0,g0) = 1.5
    c: DistanceY(g1,g1) = 1.9
    c: DistanceY(g3,g3) = 1.9
    c: DistanceX(g4,g4) = 1.5
FEATURE [PartDesign::Pocket] Pocket103
  BaseFeature = -> Pad152
  Direction = (0,0,1)
  Length = 5
  Length2 = 5
  Profile = -> Sketch252
  ReferenceAxis = -> Sketch252 [N_Axis]
  Refine = true
  Suppressed = false
  Type = 0
FEATURE [Sketcher::SketchObject] Sketch253
  ArcFitTolerance = 1e-06
  AttachmentSupport = -> [Pocket103]
  ExternalGeometry = -> [Pocket103]
  FullyConstrained = true
  MakeInternals = false
  MapMode = 5
  Placement = pos=(16,0,0) rot=(0.57735,0.57735,0.57735;2.0944rad)
  sketch-geometry (3):
    g0: LineSegment StartX=-0.05 StartY=0 StartZ=0 EndX=-0.05 EndY=1 EndZ=0
    g1: LineSegment StartX=-0.05 StartY=1 StartZ=0 EndX=0.95 EndY=0 EndZ=0
    g2: LineSegment StartX=0.95 StartY=0 StartZ=0 EndX=-0.05 EndY=0 EndZ=0
  constraints (8):
    c: Coincident(g0,g-4)
    c: Coincident(g1,g0)
    c: PointOnObject(g1,g-4)
    c: Coincident(g2,g1)
    c: Coincident(g2,g0)
    c: DistanceX(g2,g2) = 1
    c: DistanceY(g0,g0) = 1
    c: PointOnObject(g0,g-3)
FEATURE [PartDesign::Pocket] Pocket104
  BaseFeature = -> Pocket103
  Direction = (-1,0,0)
  Length = 16
  Length2 = 5
  Profile = -> Sketch253
  ReferenceAxis = -> Sketch253 [N_Axis]
  Refine = true
  Suppressed = false
  Type = 0
FEATURE [Sketcher::SketchObject] Sketch254
  ArcFitTolerance = 1e-06
  AttachmentSupport = -> [Pocket104]
  ExternalGeometry = -> [Pocket104]
  FullyConstrained = true
  MakeInternals = false
  MapMode = 5
  Placement = pos=(0,0,2) rot=(0,0,1;0rad)
  sketch-geometry (10):
    g0: LineSegment StartX=14.5 StartY=5.15 StartZ=0 EndX=13.8 EndY=5.15 EndZ=0
    g1: LineSegment StartX=13.8 StartY=5.15 StartZ=0 EndX=13.8 EndY=-0.05 EndZ=0
    g2: LineSegment StartX=13.8 StartY=-0.05 StartZ=0 EndX=16 EndY=-0.05 EndZ=0
    g3: LineSegment StartX=16 StartY=-0.05 StartZ=0 EndX=16 EndY=3.25 EndZ=0
    g4: LineSegment StartX=16 StartY=3.25 StartZ=0 EndX=14.5 EndY=5.15 EndZ=0
    g5: LineSegment StartX=1.5 StartY=5.15 StartZ=0 EndX=0 EndY=3.25 EndZ=0
    g6: LineSegment StartX=0 StartY=3.25 StartZ=0 EndX=0 EndY=-0.05 EndZ=0
    g7: LineSegment StartX=0 StartY=-0.05 StartZ=0 EndX=2.2 EndY=-0.05 EndZ=0
    g8: LineSegment StartX=2.2 StartY=-0.05 StartZ=0 EndX=2.2 EndY=5.15 EndZ=0
    g9: LineSegment StartX=2.2 StartY=5.15 StartZ=0 EndX=1.5 EndY=5.15 EndZ=0
  constraints (24):
    c: Coincident(g0,g-6)
    c: PointOnObject(g0,g-6)
    c: Coincident(g1,g0)
    c: PointOnObject(g1,g-5)
    c: Vertical(g1)
    c: Coincident(g2,g1)
    c: Coincident(g2,g-5)
    c: Coincident(g3,g2)
    c: Coincident(g3,g-4)
    c: Coincident(g4,g3)
    c: Coincident(g4,g0)
    c: DistanceX(g0,g0) = 0.7
    c: Coincident(g5,g-7)
    c: Coincident(g5,g-8)
    c: Coincident(g6,g5)
    c: Coincident(g6,g-8)
    c: Coincident(g7,g6)
    c: PointOnObject(g7,g-5)
    c: Coincident(g8,g7)
    c: PointOnObject(g8,g-6)
    c: Vertical(g8)
    c: Coincident(g9,g8)
    c: Coincident(g9,g5)
    c: DistanceX(g9,g9) = 0.7
FEATURE [PartDesign::Pad] Pad153
  BaseFeature = -> Pocket104
  Direction = (0,0,1)
  Length = 11.5
  Length2 = 10
  Profile = -> Sketch254
  ReferenceAxis = -> Sketch254 [N_Axis]
  Refine = true
  Suppressed = false
  Type = 0
FEATURE [Sketcher::SketchObject] Sketch255
  ArcFitTolerance = 1e-06
  AttachmentSupport = -> [Pad153]
  ExternalGeometry = -> [Pad153]
  FullyConstrained = true
  MakeInternals = false
  MapMode = 5
  Placement = pos=(0,0,0) rot=(1,0,0;3.14159rad)
  sketch-geometry (4):
    g0: LineSegment StartX=0 StartY=0.05 StartZ=0 EndX=0 EndY=-0.11 EndZ=0
    g1: LineSegment StartX=0 StartY=-0.11 StartZ=0 EndX=16 EndY=-0.11 EndZ=0
    g2: LineSegment StartX=16 StartY=-0.11 StartZ=0 EndX=16 EndY=0.05 EndZ=0
    g3: LineSegment StartX=16 StartY=0.05 StartZ=0 EndX=0 EndY=0.05 EndZ=0
  constraints (11):
    c: Coincident(g0,g1)
    c: Coincident(g1,g2)
    c: Coincident(g2,g3)
    c: Coincident(g3,g0)
    c: Vertical(g0)
    c: Vertical(g2)
    c: Horizontal(g1)
    c: Horizontal(g3)
    c: Coincident(g0,g-5)
    c: PointOnObject(g1,g-4)
    c: DistanceY(g2,g2) = 0.16
FEATURE [PartDesign::Pocket] Pocket105
  BaseFeature = -> Pad153
  Direction = (0,0,1)
  Length = 14
  Length2 = 5
  Profile = -> Sketch255
  ReferenceAxis = -> Sketch255 [N_Axis]
  Refine = true
  Suppressed = false
  Type = 0
FEATURE [Sketcher::SketchObject] Sketch264
  ArcFitTolerance = 1e-06
  AttachmentSupport = -> [Pocket105]
  ExternalGeometry = -> [Pocket105]
  FullyConstrained = true
  MakeInternals = false
  MapMode = 5
  Placement = pos=(3e-16,0,0) rot=(0.57735,-0.57735,-0.57735;2.0944rad)
  sketch-geometry (3):
    g0: ArcOfCircle CenterX=-5.21332 CenterY=-8.49991 CenterZ=0 NormalX=0 NormalY=0 NormalZ=1 AngleXU=0 Radius=22 StartAngle=1.33669 EndAngle=1.56792
    g1: LineSegment StartX=-5.15 StartY=13.5 StartZ=0 EndX=-0.11 EndY=13.5 EndZ=0
    g2: LineSegment StartX=-0.11 StartY=13.5 StartZ=0 EndX=-0.11 EndY=12.9 EndZ=0
  constraints (8):
    c: Coincident(g0,g-6)
    c: PointOnObject(g0,g-3)
    c: Coincident(g1,g0)
    c: Coincident(g1,g-5)
    c: Coincident(g2,g1)
    c: Coincident(g2,g0)
    c: DistanceY(g2,g2) = 0.6
    c: Radius(g0) = 22
FEATURE [PartDesign::Pocket] Pocket110
  BaseFeature = -> Pocket105
  Direction = (1,0,0)
  Length = 17
  Length2 = 5
  Profile = -> Sketch264
  ReferenceAxis = -> Sketch264 [N_Axis]
  Refine = true
  Suppressed = false
  Type = 0
FEATURE [PartDesign::Body] Body008  label="Scoop_Stop"
  AllowCompound = false
  Group = -> [Sketch251,Pad152,Sketch252,Pocket103,Sketch253,Pocket104,Sketch254,Pad153,Sketch255,Pocket105,Sketch264,Pocket110]
  Origin = -> Origin008
  Placement = pos=(-13.7,-8,0) rot=(0,0,1;1.5708rad)
  Tip = -> Pocket110
COMPONENT P5 — recipe-attached ("Canopy", modeled in this document).
Construction recipe (the document's own serialized feature program — sketch geometry with constraints, then the solid features built on it; lengths are millimeters unless a unit is written):

FEATURE [PartDesign::SubShapeBinder] Binder002
  BindCopyOnChange = 0
  BindMode = 0
  ClaimChildren = false
  Context = -> Body010 [Binder002.]
  Fuse = false
  MakeFace = true
  OffsetFill = false
  OffsetIntersection = false
  OffsetJoinType = 0
  OffsetOpenResult = false
  PartialLoad = false
  Refine = true
  Relative = true
  Support = -> [Body[Fillet001.Edge549,Fillet001.Edge558]]
  _Version = 2
FEATURE [Sketcher::SketchObject] Sketch278
  ArcFitTolerance = 1e-06
  AttachmentSupport = -> [Binder002]
  ExternalGeometry = -> [Binder002]
  FullyConstrained = true
  MakeInternals = false
  MapMode = 5
  Placement = pos=(0,0,9) rot=(0,0,1;0rad)
  sketch-geometry (1):
    g0: Circle CenterX=-33.05 CenterY=6.225 CenterZ=0 NormalX=0 NormalY=0 NormalZ=1 AngleXU=0 Radius=1.3
  constraints (3):
    c: Coincident(g0,g-3)
    c: Diameter(g-3) = 2.7
    c: Diameter(g0) = 2.6
FEATURE [PartDesign::Pad] Pad169
  Direction = (0,0,1)
  Length = 4.5
  Length2 = 10
  Profile = -> Sketch278
  ReferenceAxis = -> Sketch278 [N_Axis]
  Refine = true
  Reversed = true
  Suppressed = false
  Type = 0
FEATURE [Sketcher::SketchObject] Sketch279
  ArcFitTolerance = 1e-06
  AttachmentSupport = -> [Pad169]
  ExternalGeometry = -> [Pad169]
  FullyConstrained = true
  MakeInternals = false
  MapMode = 5
  Placement = pos=(0,0,9) rot=(0,0,1;0rad)
  sketch-geometry (4):
    g0: ArcOfCircle CenterX=-33.9 CenterY=6.225 CenterZ=0 NormalX=0 NormalY=0 NormalZ=1 AngleXU=0 Radius=1.35 StartAngle=1.5708 EndAngle=4.71239
    g1: ArcOfCircle CenterX=-32.2 CenterY=6.225 CenterZ=0 NormalX=0 NormalY=0 NormalZ=1 AngleXU=0 Radius=1.35 StartAngle=4.71239 EndAngle=7.85398
    g2: LineSegment StartX=-33.9 StartY=7.575 StartZ=0 EndX=-32.2 EndY=7.575 EndZ=0
    g3: LineSegment StartX=-33.9 StartY=4.875 StartZ=0 EndX=-32.2 EndY=4.875 EndZ=0
  constraints (10):
    c: Tangent(g0,g2) = 1.5708
    c: Tangent(g0,g3) = -1.5708
    c: Tangent(g1,g2) = 1.5708
    c: Tangent(g1,g3) = -1.5708
    c: Equal(g0,g1)
    c: Horizontal(g3)
    c: Diameter(g0) = 2.7
    c: DistanceX(g0,g1) = 1.7
    c: DistanceX(g0,g-3) = 0.85
    c: DistanceY(g-3,g0) = 1.35
FEATURE [PartDesign::Pad] Pad170
  BaseFeature = -> Pad169
  Direction = (0,0,1)
  Length = 4.7
  Length2 = 10
  Profile = -> Sketch279
  ReferenceAxis = -> Sketch279 [N_Axis]
  Refine = true
  Suppressed = false
  Type = 0
FEATURE [Sketcher::SketchObject] Sketch280
  ArcFitTolerance = 1e-06
  AttachmentOffset = pos=(0,0,10) rot=(0,0,1;0rad)
  AttachmentSupport = -> [Pad170]
  ExternalGeometry = -> [Pad170]
  FullyConstrained = true
  MakeInternals = false
  MapMode = 5
  Placement = pos=(0,0,23.7) rot=(0,0,1;0rad)
  sketch-geometry (4):
    g0: ArcOfCircle CenterX=-38.7 CenterY=6.225 CenterZ=0 NormalX=0 NormalY=0 NormalZ=1 AngleXU=0 Radius=1.35 StartAngle=1.5708 EndAngle=4.71239
    g1: ArcOfCircle CenterX=-27.4 CenterY=6.225 CenterZ=0 NormalX=0 NormalY=0 NormalZ=1 AngleXU=0 Radius=1.35 StartAngle=4.71239 EndAngle=7.85398
    g2: LineSegment StartX=-38.7 StartY=7.575 StartZ=0 EndX=-27.4 EndY=7.575 EndZ=0
    g3: LineSegment StartX=-38.7 StartY=4.875 StartZ=0 EndX=-27.4 EndY=4.875 EndZ=0
  constraints (13):
    c: Tangent(g0,g2) = 1.5708
    c: Tangent(g0,g3) = -1.5708
    c: Tangent(g1,g2) = 1.5708
    c: Tangent(g1,g3) = -1.5708
    c: Equal(g0,g1)
    c: Horizontal(g2)
    c: PointOnObject(g-4,g2)
    c: PointOnObject(g-5,g3)
    c: DistanceX(g0,g1) = 11.3
    c: Diameter(g0) = 2.7
    c: DistanceX(g-4,g-6) = 1.7
    c: DistanceX(g0,g-4) = 4.8
    c: DistanceX(g-6,g1) = 4.8
FEATURE [PartDesign::AdditiveLoft] AdditiveLoft
  BaseFeature = -> Pad170
  Closed = false
  Profile = -> Pad170 [Face8]
  Refine = true
  Ruled = false
  Sections = -> [Sketch280]
  Suppressed = false
FEATURE [Sketcher::SketchObject] Sketch281
  ArcFitTolerance = 1e-06
  AttachmentSupport = -> [AdditiveLoft]
  ExternalGeometry = -> [AdditiveLoft]
  FullyConstrained = true
  MakeInternals = false
  MapMode = 5
  Placement = pos=(0,0,23.7) rot=(0,0,1;0rad)
  sketch-geometry (8):
    g0: LineSegment StartX=-43.2 StartY=9.25 StartZ=0 EndX=-43.2 EndY=-9.25 EndZ=0
    g1: LineSegment StartX=-43.2 StartY=-9.25 StartZ=0 EndX=-22.9 EndY=-9.25 EndZ=0
    g2: LineSegment StartX=-22.9 StartY=-9.25 StartZ=0 EndX=-22.9 EndY=9.25 EndZ=0
    g3: LineSegment StartX=-22.9 StartY=9.25 StartZ=0 EndX=-43.2 EndY=9.25 EndZ=0
    g4: ArcOfCircle CenterX=-38.7 CenterY=-6.225 CenterZ=0 NormalX=0 NormalY=0 NormalZ=1 AngleXU=0 Radius=1.35 StartAngle=1.5708 EndAngle=4.71239
    g5: ArcOfCircle CenterX=-27.4 CenterY=-6.225 CenterZ=0 NormalX=0 NormalY=0 NormalZ=1 AngleXU=0 Radius=1.35 StartAngle=4.71239 EndAngle=7.85398
    g6: LineSegment StartX=-38.7 StartY=-4.875 StartZ=0 EndX=-27.4 EndY=-4.875 EndZ=0
    g7: LineSegment StartX=-38.7 StartY=-7.575 StartZ=0 EndX=-27.4 EndY=-7.575 EndZ=0
  constraints (25):
    c: Coincident(g0,g1)
    c: Coincident(g1,g2)
    c: Coincident(g2,g3)
    c: Coincident(g3,g0)
    c: Vertical(g0)
    c: Vertical(g2)
    c: Horizontal(g1)
    c: Horizontal(g3)
    c: DistanceX(g3,g3) = 20.3
    c: DistanceY(g0,g0) = 18.5
    c: Tangent(g4,g6) = 1.5708
    c: Tangent(g4,g7) = -1.5708
    c: Tangent(g5,g6) = 1.5708
    c: Tangent(g5,g7) = -1.5708
    c: Equal(g4,g5)
    c: Horizontal(g6)
    c: DistanceY(g4,g-3) = 12.45
    c: Diameter(g-3) = 2.7
    c: Diameter(g4) = 2.7
    c: DistanceX(g-3,g4) = 0
    c: DistanceX(g5,g-5) = 0
    c: DistanceY(g-3,g0) = 3.025
    c: DistanceY(g0,g4) = 3.025
    c: DistanceX(g0,g-3) = 4.5
    c: DistanceX(g5,g1) = 4.5
FEATURE [PartDesign::Pad] Pad171
  BaseFeature = -> AdditiveLoft
  Direction = (0,0,1)
  Length = 1.6
  Length2 = 10
  Profile = -> Sketch281 [Edge1,Edge4,Edge3,Edge2]
  ReferenceAxis = -> Sketch281 [N_Axis]
  Refine = true
  Suppressed = false
  Type = 0
FEATURE [Sketcher::SketchObject] Sketch282
  ArcFitTolerance = 1e-06
  AttachmentSupport = -> [Pad171]
  ExternalGeometry = -> [Sketch281]
  FullyConstrained = false
  MakeInternals = false
  MapMode = 5
  Placement = pos=(0,0,23.7) rot=(1,0,0;3.14159rad)
  sketch-geometry (4):
    g0: LineSegment StartX=-38.7 StartY=7.575 StartZ=0 EndX=-27.4 EndY=7.575 EndZ=0
    g1: LineSegment StartX=-27.4 StartY=4.875 StartZ=0 EndX=-38.7 EndY=4.875 EndZ=0
    g2: ArcOfCircle CenterX=-38.7 CenterY=6.225 CenterZ=0 NormalX=0 NormalY=0 NormalZ=1 AngleXU=0 Radius=1.35 StartAngle=1.5708 EndAngle=4.71239
    g3: ArcOfCircle CenterX=-27.4 CenterY=6.225 CenterZ=0 NormalX=0 NormalY=0 NormalZ=1 AngleXU=0 Radius=1.35 StartAngle=4.71239 EndAngle=7.85398
  constraints (10):
    c: PointOnObject(g0,g-6)
    c: Coincident(g0,g-4)
    c: Horizontal(g0)
    c: Coincident(g1,g-5)
    c: Coincident(g1,g-6)
    c: Coincident(g2,g0)
    c: Coincident(g2,g1)
    c: Coincident(g3,g0)
    c: Coincident(g3,g1)
    c: Tangent(g3,g-3)
FEATURE [Sketcher::SketchObject] Sketch283
  ArcFitTolerance = 1e-06
  AttachmentOffset = pos=(0,0,10) rot=(0,0,1;0rad)
  AttachmentSupport = -> [Pad171]
  ExternalGeometry = -> [Sketch282]
  FullyConstrained = true
  MakeInternals = false
  MapMode = 5
  Placement = pos=(0,0,13.7) rot=(1,0,0;3.14159rad)
  sketch-geometry (4):
    g0: ArcOfCircle CenterX=-33.9 CenterY=6.225 CenterZ=0 NormalX=0 NormalY=0 NormalZ=1 AngleXU=0 Radius=1.35 StartAngle=1.5708 EndAngle=4.71239
    g1: ArcOfCircle CenterX=-32.2 CenterY=6.225 CenterZ=0 NormalX=0 NormalY=0 NormalZ=1 AngleXU=0 Radius=1.35 StartAngle=4.71239 EndAngle=7.85398
    g2: LineSegment StartX=-32.2 StartY=7.575 StartZ=0 EndX=-33.9 EndY=7.575 EndZ=0
    g3: LineSegment StartX=-32.2 StartY=4.875 StartZ=0 EndX=-33.9 EndY=4.875 EndZ=0
  constraints (15):
    c: PointOnObject(g0,g-3)
    c: PointOnObject(g0,g-4)
    c: PointOnObject(g1,g-3)
    c: Coincident(g2,g1)
    c: Coincident(g2,g0)
    c: Coincident(g3,g1)
    c: Coincident(g3,g0)
    c: Horizontal(g3)
    c: DistanceX(g1,g1) = 0
    c: DistanceX(g1,g1) = 0
    c: DistanceX(g0,g0) = 0
    c: DistanceX(g0,g0) = 0
    c: DistanceX(g2,g2) = 1.7
    c: DistanceX(g1,g-3) = 4.8
    c: DistanceX(g-3,g0) = 4.8
FEATURE [PartDesign::AdditiveLoft] AdditiveLoft001
  BaseFeature = -> Pad171
  Closed = false
  Profile = -> Sketch282
  Refine = true
  Ruled = false
  Sections = -> [Sketch283]
  Suppressed = false
FEATURE [PartDesign::Pad] Pad172
  BaseFeature = -> AdditiveLoft001
  Direction = (0,0,-1)
  Length = 4.7
  Length2 = 10
  Profile = -> Sketch283
  ReferenceAxis = -> Sketch283 [N_Axis]
  Refine = true
  Suppressed = false
  Type = 0
FEATURE [Sketcher::SketchObject] Sketch284
  ArcFitTolerance = 1e-06
  AttachmentSupport = -> [Pad172]
  ExternalGeometry = -> [Pad172]
  FullyConstrained = true
  MakeInternals = false
  MapMode = 5
  Placement = pos=(0,0,9) rot=(1,0,0;3.14159rad)
  sketch-geometry (1):
    g0: Circle CenterX=-33.05 CenterY=6.225 CenterZ=0 NormalX=0 NormalY=0 NormalZ=1 AngleXU=0 Radius=1.3
  constraints (6):
    c: Diameter(g-7) = 2.6
    c: Diameter(g0) = 2.6
    c: DistanceX(g-8,g-7) = 0.85
    c: DistanceX(g-4,g0) = 0.85
    c: DistanceY(g-7,g-8) = 1.35
    c: DistanceY(g0,g-4) = 1.35
FEATURE [PartDesign::Pad] Pad173
  BaseFeature = -> Pad172
  Direction = (0,0,-1)
  Length = 4.5
  Length2 = 10
  Profile = -> Sketch284
  ReferenceAxis = -> Sketch284 [N_Axis]
  Refine = true
  Suppressed = false
  Type = 0
FEATURE [PartDesign::Fillet] Fillet010
  Base = -> Pad173 [Edge38,Edge26,Edge34,Edge24,Edge33,Edge32,Edge37,Edge39,Edge36,Edge27,Edge35,Edge25]
  BaseFeature = -> Pad173
  Radius = 0.5
  Refine = true
  SupportTransform = false
  Suppressed = false
  UseAllEdges = false
FEATURE [PartDesign::Body] Body010  label="Canopy"
  AllowCompound = false
  Group = -> [Binder002,Sketch278,Pad169,Sketch279,Pad170,Sketch280,AdditiveLoft,Sketch281,Pad171,Sketch282,Sketch283,AdditiveLoft001,Pad172,Sketch284,Pad173,Fillet010]
  Origin = -> Origin010
  Tip = -> Fillet010
COMPONENT P6 — recipe-attached ("Left_Foot", modeled in this document).
Construction recipe (the document's own serialized feature program — sketch geometry with constraints, then the solid features built on it; lengths are millimeters unless a unit is written):

FEATURE [Sketcher::SketchObject] Sketch285
  ArcFitTolerance = 1e-06
  AttachmentSupport = -> [XY_Plane011]
  FullyConstrained = true
  MakeInternals = false
  MapMode = 5
  sketch-geometry (4):
    g0: LineSegment StartX=0 StartY=0 StartZ=0 EndX=31.7 EndY=0 EndZ=0
    g1: LineSegment StartX=31.7 StartY=0 StartZ=0 EndX=31.7 EndY=11.1 EndZ=0
    g2: LineSegment StartX=31.7 StartY=11.1 StartZ=0 EndX=0 EndY=11.1 EndZ=0
    g3: LineSegment StartX=0 StartY=11.1 StartZ=0 EndX=0 EndY=0 EndZ=0
  constraints (11):
    c: Coincident(g0,g1)
    c: Coincident(g1,g2)
    c: Coincident(g2,g3)
    c: Coincident(g3,g0)
    c: Horizontal(g0)
    c: Horizontal(g2)
    c: Vertical(g1)
    c: Vertical(g3)
    c: Coincident(g0,g-1)
    c: DistanceY(g1,g1) = 11.1
    c: DistanceX(g2,g2) = 31.7
FEATURE [PartDesign::Pad] Pad174
  Direction = (0,0,1)
  Length = 1.5
  Length2 = 10
  Profile = -> Sketch285
  ReferenceAxis = -> Sketch285 [N_Axis]
  Refine = true
  Reversed = true
  Suppressed = false
  Type = 0
FEATURE [Sketcher::SketchObject] Sketch286
  ArcFitTolerance = 1e-06
  AttachmentSupport = -> [Pad174]
  ExternalGeometry = -> [Pad174]
  FullyConstrained = true
  MakeInternals = false
  MapMode = 5
  Placement = pos=(0,0,0) rot=(1,0,0;1.5708rad)
  sketch-geometry (10):
    g0: LineSegment StartX=0 StartY=-1.5 StartZ=0 EndX=0 EndY=-14.5 EndZ=0
    g1: LineSegment StartX=0 StartY=-14.5 StartZ=0 EndX=-2.1 EndY=-14.5 EndZ=0
    g2: LineSegment StartX=-2.1 StartY=-14.5 StartZ=0 EndX=-2.1 EndY=-18 EndZ=0
    g3: LineSegment StartX=-2.1 StartY=-18 StartZ=0 EndX=18.95 EndY=-18 EndZ=0
    g4: LineSegment StartX=18.95 StartY=-18 StartZ=0 EndX=18.95 EndY=-7.5 EndZ=0
    g5: LineSegment StartX=18.95 StartY=-7.5 StartZ=0 EndX=30.2 EndY=-7.5 EndZ=0
    g6: LineSegment StartX=30.2 StartY=-7.5 StartZ=0 EndX=30.2 EndY=-8 EndZ=0
    g7: LineSegment StartX=30.2 StartY=-8 StartZ=0 EndX=31.7 EndY=-8 EndZ=0
    g8: LineSegment StartX=31.7 StartY=-8 StartZ=0 EndX=31.7 EndY=-1.5 EndZ=0
    g9: LineSegment StartX=0 StartY=-1.5 StartZ=0 EndX=31.7 EndY=-1.5 EndZ=0
  constraints (28):
    c: Coincident(g0,g-3)
    c: PointOnObject(g0,g-2)
    c: Coincident(g1,g0)
    c: Horizontal(g1)
    c: Coincident(g2,g1)
    c: Coincident(g3,g2)
    c: Horizontal(g3)
    c: Coincident(g4,g3)
    c: Vertical(g4)
    c: Coincident(g5,g4)
    c: Horizontal(g5)
    c: Coincident(g6,g5)
    c: Vertical(g6)
    c: Coincident(g7,g6)
    c: Horizontal(g7)
    c: Coincident(g8,g7)
    c: Coincident(g8,g-3)
    c: Vertical(g8)
    c: DistanceY(g2,g0) = 16.5
    c: Vertical(g2)
    c: DistanceY(g2,g2) = 3.5
    c: DistanceY(g4,g4) = 10.5
    c: DistanceX(g4,g7) = 12.75
    c: DistanceY(g6,g6) = 0.5
    c: DistanceX(g7,g7) = 1.5
    c: Coincident(g9,g0)
    c: Coincident(g9,g8)
    c: DistanceX(g1,g1) = 2.1
FEATURE [PartDesign::Pad] Pad175
  BaseFeature = -> Pad174
  Direction = (0,-1,2e-16)
  Length = 1.75
  Length2 = 10
  Profile = -> Sketch286
  ReferenceAxis = -> Sketch286 [N_Axis]
  Refine = true
  Reversed = true
  Suppressed = false
  Type = 0
FEATURE [Sketcher::SketchObject] Sketch287
  ArcFitTolerance = 1e-06
  AttachmentSupport = -> [Pad175]
  ExternalGeometry = -> [Pad175]
  FullyConstrained = true
  MakeInternals = false
  MapMode = 5
  Placement = pos=(0,1.75,-4e-16) rot=(0,0.707107,0.707107;3.14159rad)
  sketch-geometry (4):
    g0: LineSegment StartX=-18.95 StartY=-18 StartZ=0 EndX=-16.95 EndY=-18 EndZ=0
    g1: LineSegment StartX=-16.95 StartY=-18 StartZ=0 EndX=-16.95 EndY=-1.5 EndZ=0
    g2: LineSegment StartX=-16.95 StartY=-1.5 StartZ=0 EndX=-18.95 EndY=-1.5 EndZ=0
    g3: LineSegment StartX=-18.95 StartY=-1.5 StartZ=0 EndX=-18.95 EndY=-18 EndZ=0
  constraints (11):
    c: Coincident(g0,g1)
    c: Coincident(g1,g2)
    c: Coincident(g2,g3)
    c: Coincident(g3,g0)
    c: Horizontal(g0)
    c: Horizontal(g2)
    c: Vertical(g1)
    c: Vertical(g3)
    c: Coincident(g0,g-4)
    c: PointOnObject(g1,g-5)
    c: DistanceX(g0,g0) = 2
FEATURE [PartDesign::Pad] Pad176
  BaseFeature = -> Pad175
  Direction = (0,1,-2e-16)
  Length = 1.25
  Length2 = 10
  Profile = -> Sketch287
  ReferenceAxis = -> Sketch287 [N_Axis]
  Refine = true
  Suppressed = false
  Type = 0
FEATURE [Sketcher::SketchObject] Sketch288
  ArcFitTolerance = 1e-06
  AttachmentSupport = -> [Pad176]
  ExternalGeometry = -> [Pad176]
  FullyConstrained = true
  MakeInternals = false
  MapMode = 5
  Placement = pos=(0,11.1,0) rot=(0,0.707107,0.707107;3.14159rad)
  sketch-geometry (5):
    g0: LineSegment StartX=-31.7 StartY=-1.5 StartZ=0 EndX=0 EndY=-1.5 EndZ=0
    g1: LineSegment StartX=0 StartY=-1.5 StartZ=0 EndX=0 EndY=-18 EndZ=0
    g2: LineSegment StartX=0 StartY=-18 StartZ=0 EndX=-27.2 EndY=-18 EndZ=0
    g3: LineSegment StartX=-27.2 StartY=-18 StartZ=0 EndX=-31.7 EndY=-21 EndZ=0
    g4: LineSegment StartX=-31.7 StartY=-1.5 StartZ=0 EndX=-31.7 EndY=-21 EndZ=0
  constraints (13):
    c: Coincident(g0,g-3)
    c: Coincident(g0,g-3)
    c: Coincident(g1,g0)
    c: PointOnObject(g1,g-4)
    c: Vertical(g1)
    c: Coincident(g2,g1)
    c: Horizontal(g2)
    c: Coincident(g3,g2)
    c: Coincident(g4,g0)
    c: Coincident(g4,g3)
    c: Vertical(g4)
    c: DistanceX(g3,g2) = 4.5
    c: DistanceY(g3,g2) = 3
FEATURE [PartDesign::Pad] Pad177
  BaseFeature = -> Pad176
  Direction = (0,1,-2e-16)
  Length = 1.4
  Length2 = 10
  Profile = -> Sketch288
  ReferenceAxis = -> Sketch288 [N_Axis]
  Refine = true
  Reversed = true
  Suppressed = false
  Type = 0
FEATURE [Sketcher::SketchObject] Sketch289
  ArcFitTolerance = 1e-06
  AttachmentSupport = -> [Pad177]
  ExternalGeometry = -> [Pad177]
  FullyConstrained = true
  MakeInternals = false
  MapMode = 5
  Placement = pos=(31.7,0,0) rot=(0.57735,0.57735,0.57735;2.0944rad)
  sketch-geometry (4):
    g0: LineSegment StartX=1.75 StartY=-1.5 StartZ=0 EndX=1.75 EndY=-8 EndZ=0
    g1: LineSegment StartX=1.75 StartY=-8 StartZ=0 EndX=9.7 EndY=-8 EndZ=0
    g2: LineSegment StartX=9.7 StartY=-8 StartZ=0 EndX=9.7 EndY=-1.5 EndZ=0
    g3: LineSegment StartX=9.7 StartY=-1.5 StartZ=0 EndX=1.75 EndY=-1.5 EndZ=0
  constraints (10):
    c: Coincident(g0,g1)
    c: Coincident(g1,g2)
    c: Coincident(g2,g3)
    c: Coincident(g3,g0)
    c: Vertical(g2)
    c: Horizontal(g1)
    c: Horizontal(g3)
    c: Coincident(g0,g-5)
    c: PointOnObject(g1,g-4)
    c: Coincident(g0,g-5)
FEATURE [PartDesign::Pad] Pad178
  BaseFeature = -> Pad177
  Direction = (1,0,0)
  Length = 1.5
  Length2 = 10
  Profile = -> Sketch289
  ReferenceAxis = -> Sketch289 [N_Axis]
  Refine = true
  Reversed = true
  Suppressed = false
  Type = 0
FEATURE [Sketcher::SketchObject] Sketch290
  ArcFitTolerance = 1e-06
  AttachmentSupport = -> [Pad178]
  ExternalGeometry = -> [Pad178]
  FullyConstrained = true
  MakeInternals = false
  MapMode = 5
  Placement = pos=(0,0,0) rot=(0.57735,-0.57735,-0.57735;2.0944rad)
  sketch-geometry (6):
    g0: LineSegment StartX=-9.7 StartY=-1.5 StartZ=0 EndX=-9.7 EndY=-18 EndZ=0
    g1: LineSegment StartX=-1.75 StartY=-7.5 StartZ=0 EndX=-1.75 EndY=-1.5 EndZ=0
    g2: LineSegment StartX=-1.75 StartY=-1.5 StartZ=0 EndX=-9.7 EndY=-1.5 EndZ=0
    g3: LineSegment StartX=-9.7 StartY=-18 StartZ=0 EndX=-6.6 EndY=-18 EndZ=0
    g4: LineSegment StartX=-6.6 StartY=-18 StartZ=0 EndX=-6.6 EndY=-7.5 EndZ=0
    g5: LineSegment StartX=-1.75 StartY=-7.5 StartZ=0 EndX=-6.6 EndY=-7.5 EndZ=0
  constraints (17):
    c: Coincident(g1,g2)
    c: Coincident(g2,g0)
    c: Vertical(g1)
    c: Horizontal(g2)
    c: Coincident(g0,g-5)
    c: PointOnObject(g1,g-3)
    c: Coincident(g0,g-5)
    c: Coincident(g3,g0)
    c: Horizontal(g3)
    c: Coincident(g4,g3)
    c: Vertical(g4)
    c: DistanceY(g1,g1) = 6
    c: Coincident(g5,g1)
    c: Coincident(g5,g4)
    c: Horizontal(g5)
    c: DistanceX(g3,g3) = 3.1
    c: DistanceX(g-6,g-6) = 1.4
FEATURE [PartDesign::Pad] Pad179
  BaseFeature = -> Pad178
  Direction = (-1,0,0)
  Length = 1.5
  Length2 = 10
  Profile = -> Sketch290
  ReferenceAxis = -> Sketch290 [N_Axis]
  Refine = true
  Reversed = true
  Suppressed = false
  Type = 0
FEATURE [Sketcher::SketchObject] Sketch291
  ArcFitTolerance = 1e-06
  AttachmentSupport = -> [Pad179]
  ExternalGeometry = -> [Pad179]
  FullyConstrained = true
  MakeInternals = false
  MapMode = 5
  Placement = pos=(0,0,0) rot=(0.57735,-0.57735,-0.57735;2.0944rad)
  sketch-geometry (4):
    g0: LineSegment StartX=-6.6 StartY=-18 StartZ=0 EndX=-6.6 EndY=-14.5 EndZ=0
    g1: LineSegment StartX=-6.6 StartY=-14.5 StartZ=0 EndX=-11.1 EndY=-14.5 EndZ=0
    g2: LineSegment StartX=-11.1 StartY=-14.5 StartZ=0 EndX=-11.1 EndY=-18 EndZ=0
    g3: LineSegment StartX=-11.1 StartY=-18 StartZ=0 EndX=-6.6 EndY=-18 EndZ=0
  constraints (12):
    c: Coincident(g0,g1)
    c: Coincident(g1,g2)
    c: Coincident(g2,g3)
    c: Coincident(g3,g0)
    c: Vertical(g0)
    c: Vertical(g2)
    c: Horizontal(g1)
    c: Horizontal(g3)
    c: Coincident(g0,g-4)
    c: PointOnObject(g1,g-5)
    c: DistanceY(g-6,g-6) = 3.5
    c: DistanceY(g0,g0) = 3.5
FEATURE [PartDesign::Pad] Pad180
  BaseFeature = -> Pad179
  Direction = (-1,0,0)
  Length = 2.1
  Length2 = 10
  Profile = -> Sketch291
  ReferenceAxis = -> Sketch291 [N_Axis]
  Refine = true
  Suppressed = false
  Type = 0
FEATURE [Sketcher::SketchObject] Sketch292
  ArcFitTolerance = 1e-06
  AttachmentSupport = -> [Pad180]
  ExternalGeometry = -> [Pad180]
  FullyConstrained = true
  MakeInternals = false
  MapMode = 5
  Placement = pos=(0,0,-18) rot=(1,0,0;3.14159rad)
  sketch-geometry (6):
    g0: LineSegment StartX=-1.25 StartY=-14.8 StartZ=0 EndX=2.95 EndY=-14.8 EndZ=0
    g1: LineSegment StartX=3.8 StartY=-11.1 StartZ=0 EndX=-2.1 EndY=-11.1 EndZ=0
    g2: LineSegment StartX=-2.1 StartY=-11.1 StartZ=0 EndX=-2.1 EndY=-12.6 EndZ=0
    g3: LineSegment StartX=-2.1 StartY=-12.6 StartZ=0 EndX=-1.25 EndY=-14.8 EndZ=0
    g4: LineSegment StartX=2.95 StartY=-14.8 StartZ=0 EndX=3.8 EndY=-12.6 EndZ=0
    g5: LineSegment StartX=3.8 StartY=-12.6 StartZ=0 EndX=3.8 EndY=-11.1 EndZ=0
  constraints (17):
    c: Horizontal(g0)
    c: Coincident(g2,g1)
    c: Vertical(g2)
    c: Coincident(g3,g2)
    c: Coincident(g3,g0)
    c: Coincident(g4,g0)
    c: Coincident(g5,g4)
    c: PointOnObject(g5,g-3)
    c: Vertical(g5)
    c: Coincident(g1,g5)
    c: DistanceX(g1,g1) = 5.9
    c: DistanceX(g0,g0) = 4.2
    c: DistanceY(g0,g1) = 3.7
    c: Coincident(g1,g-3)
    c: DistanceY(g2,g2) = 1.5
    c: DistanceY(g5,g5) = 1.5
    c: DistanceX(g2,g0) = 0.85
FEATURE [PartDesign::Pad] Pad181
  BaseFeature = -> Pad180
  Direction = (0,0,-1)
  Length = 3.5
  Length2 = 10
  Profile = -> Sketch292
  ReferenceAxis = -> Sketch292 [N_Axis]
  Refine = true
  Reversed = true
  Suppressed = false
  Type = 0
FEATURE [Sketcher::SketchObject] Sketch293
  ArcFitTolerance = 1e-06
  AttachmentSupport = -> [Pad181]
  ExternalGeometry = -> [Pad181]
  FullyConstrained = true
  MakeInternals = false
  MapMode = 5
  Placement = pos=(0,11.1,0) rot=(0,0.707107,0.707107;3.14159rad)
  sketch-geometry (1):
    g0: Circle CenterX=-6.15 CenterY=-11.45 CenterZ=0 NormalX=0 NormalY=0 NormalZ=1 AngleXU=0 Radius=1.95
  constraints (3):
    c: Diameter(g0) = 3.9
    c: DistanceX(g0,g-1) = 6.15
    c: DistanceY(g-4,g0) = 6.55
FEATURE [PartDesign::Pad] Pad182
  BaseFeature = -> Pad181
  Direction = (0,1,-2e-16)
  Length = 3.1
  Length2 = 10
  Profile = -> Sketch293
  ReferenceAxis = -> Sketch293 [N_Axis]
  Refine = true
  Suppressed = false
  Type = 0
FEATURE [Sketcher::SketchObject] Sketch294
  ArcFitTolerance = 1e-06
  AttachmentSupport = -> [Pad182]
  ExternalGeometry = -> [Pad182]
  FullyConstrained = true
  MakeInternals = false
  MapMode = 5
  Placement = pos=(4.3e-15,14.2,-7.5e-15) rot=(0,0.707107,0.707107;3.14159rad)
  sketch-geometry (1):
    g0: Circle CenterX=-6.15 CenterY=-11.45 CenterZ=0 NormalX=0 NormalY=0 NormalZ=1 AngleXU=0 Radius=0.9
  constraints (2):
    c: Coincident(g0,g-3)
    c: Diameter(g0) = 1.8
FEATURE [PartDesign::Pocket] Pocket114
  BaseFeature = -> Pad182
  Direction = (0,-1,2e-16)
  Length = 16
  Length2 = 5
  Profile = -> Sketch294
  ReferenceAxis = -> Sketch294 [N_Axis]
  Refine = true
  Suppressed = false
  Type = 0
FEATURE [Sketcher::SketchObject] Sketch295
  ArcFitTolerance = 1e-06
  AttachmentSupport = -> [Pocket114]
  ExternalGeometry = -> [Pocket114]
  FullyConstrained = true
  MakeInternals = false
  MapMode = 5
  Placement = pos=(0,11.1,0) rot=(0,0.707107,0.707107;3.14159rad)
  sketch-geometry (4):
    g0: LineSegment StartX=-7.6 StartY=-10.1462 StartZ=0 EndX=-7.6 EndY=-4.49617 EndZ=0
    g1: LineSegment StartX=-4.7 StartY=-10.1462 StartZ=0 EndX=-4.7 EndY=-4.49616 EndZ=0
    g2: ArcOfCircle CenterX=-6.15 CenterY=-4.49616 CenterZ=0 NormalX=0 NormalY=0 NormalZ=1 AngleXU=0 Radius=1.45 StartAngle=0 EndAngle=3.1416
    g3: ArcOfCircle CenterX=-6.15 CenterY=-11.45 CenterZ=0 NormalX=0 NormalY=0 NormalZ=1 AngleXU=0 Radius=1.95 StartAngle=0.732373 EndAngle=2.40922
  constraints (13):
    c: PointOnObject(g0,g-3)
    c: Vertical(g0)
    c: Vertical(g1)
    c: Coincident(g2,g0)
    c: Coincident(g2,g1)
    c: Diameter(g2) = 2.9
    c: Coincident(g3,g0)
    c: Coincident(g3,g1)
    c: Coincident(g3,g-3)
    c: DistanceX(g0,g3) = 1.45
    c: DistanceX(g3,g1) = 1.45
    c: DistanceY(g1,g2) = 0
    c: DistanceY(g1,g2) = 5.65
FEATURE [PartDesign::Pad] Pad183
  BaseFeature = -> Pocket114
  Direction = (0,1,-2e-16)
  Length = 2
  Length2 = 10
  Profile = -> Sketch295
  ReferenceAxis = -> Sketch295 [N_Axis]
  Refine = true
  Suppressed = false
  Type = 0
FEATURE [Sketcher::SketchObject] Sketch296
  ArcFitTolerance = 1e-06
  AttachmentSupport = -> [Pad183]
  ExternalGeometry = -> [Pad183]
  FullyConstrained = true
  MakeInternals = false
  MapMode = 5
  Placement = pos=(0,11.1,0) rot=(0,0.707107,0.707107;3.14159rad)
  sketch-geometry (8):
    g0: LineSegment StartX=-31.7 StartY=-7.55 StartZ=0 EndX=-31.7 EndY=1.5 EndZ=0
    g1: ArcOfCircle CenterX=-31.7 CenterY=0 CenterZ=0 NormalX=0 NormalY=0 NormalZ=1 AngleXU=0 Radius=1.5 StartAngle=0 EndAngle=1.5708
    g2: LineSegment StartX=-30.2 StartY=0 StartZ=0 EndX=-24 EndY=0 EndZ=0
    g3: ArcOfCircle CenterX=-24 CenterY=-1 CenterZ=0 NormalX=0 NormalY=0 NormalZ=1 AngleXU=0 Radius=1 StartAngle=4.71239 EndAngle=7.85398
    g4: LineSegment StartX=-24 StartY=-2 StartZ=0 EndX=-26.3 EndY=-2 EndZ=0
    g5: LineSegment StartX=-26.3 StartY=-2 StartZ=0 EndX=-30.2 EndY=-5.9 EndZ=0
    g6: LineSegment StartX=-30.2 StartY=-5.9 StartZ=0 EndX=-30.2 EndY=-7.55 EndZ=0
    g7: ArcOfCircle CenterX=-30.95 CenterY=-7.55 CenterZ=0 NormalX=0 NormalY=0 NormalZ=1 AngleXU=0 Radius=0.75 StartAngle=3.14159 EndAngle=6.28319
  constraints (26):
    c: PointOnObject(g0,g-3)
    c: Vertical(g0)
    c: Coincident(g1,g0)
    c: PointOnObject(g1,g-4)
    c: Coincident(g2,g1)
    c: PointOnObject(g2,g-4)
    c: Coincident(g3,g2)
    c: Coincident(g4,g3)
    c: Horizontal(g4)
    c: Coincident(g5,g4)
    c: Coincident(g6,g5)
    c: Coincident(g7,g0)
    c: Coincident(g7,g6)
    c: Diameter(g7) = 1.5
    c: Radius(g1) = 1.5
    c: Diameter(g3) = 2
    c: Angle(g5,g4) = 2.35619
    c: Vertical(g6)
    c: Coincident(g1,g-4)
    c: DistanceX(g0,g2) = 7.7
    c: DistanceX(g2,g3) = 0
    c: DistanceX(g3,g3) = 0
    c: DistanceY(g0,g0) = 9.05
    c: DistanceY(g6,g7) = 0
    c: DistanceY(g0,g7) = 0
    c: DistanceX(g4,g3) = 2.3
FEATURE [PartDesign::Pad] Pad184
  BaseFeature = -> Pad183
  Direction = (0,1,-2e-16)
  Length = 5
  Length2 = 10
  Profile = -> Sketch296
  ReferenceAxis = -> Sketch296 [N_Axis]
  Refine = true
  Suppressed = false
  Type = 0
FEATURE [PartDesign::Pad] Pad185
  BaseFeature = -> Pad184
  Direction = (0,-1,0)
  Length = 4.8
  Length2 = 10
  Profile = -> Pad184 [Face1]
  Refine = true
  Suppressed = false
  Type = 0
FEATURE [Sketcher::SketchObject] Sketch297
  ArcFitTolerance = 1e-06
  AttachmentSupport = -> [Pad185]
  ExternalGeometry = -> [Pad185]
  FullyConstrained = true
  MakeInternals = false
  MapMode = 5
  Placement = pos=(0,0,0) rot=(1,0,0;1.5708rad)
  sketch-geometry (1):
    g0: Circle CenterX=6.15 CenterY=-11.45 CenterZ=0 NormalX=0 NormalY=0 NormalZ=1 AngleXU=0 Radius=2.7
  constraints (2):
    c: Coincident(g0,g-3)
    c: Diameter(g0) = 5.4
FEATURE [PartDesign::Pocket] Pocket115
  BaseFeature = -> Pad185
  Direction = (0,1,-2e-16)
  Length = 0.5
  Length2 = 5
  Profile = -> Sketch297
  ReferenceAxis = -> Sketch297 [N_Axis]
  Refine = true
  Suppressed = false
  Type = 0
FEATURE [Sketcher::SketchObject] Sketch298
  ArcFitTolerance = 1e-06
  AttachmentOffset = pos=(0,0,-1) rot=(0,0,1;0rad)
  AttachmentSupport = -> [Pocket115]
  ExternalGeometry = -> [Pocket115]
  FullyConstrained = true
  MakeInternals = false
  MapMode = 5
  Placement = pos=(0,10.1,2e-16) rot=(0,0.707107,0.707107;3.14159rad)
  sketch-geometry (4):
    g0: ArcOfCircle CenterX=-14.4 CenterY=-17.6 CenterZ=0 NormalX=0 NormalY=0 NormalZ=1 AngleXU=0 Radius=3 StartAngle=5e-16 EndAngle=3.14159
    g1: ArcOfCircle CenterX=-14.4 CenterY=-21 CenterZ=0 NormalX=0 NormalY=0 NormalZ=1 AngleXU=0 Radius=3 StartAngle=3.14159 EndAngle=6.28319
    g2: LineSegment StartX=-11.4 StartY=-17.6 StartZ=0 EndX=-11.4 EndY=-21 EndZ=0
    g3: LineSegment StartX=-17.4 StartY=-17.6 StartZ=0 EndX=-17.4 EndY=-21 EndZ=0
  constraints (10):
    c: Tangent(g0,g2) = 1.5708
    c: Tangent(g0,g3) = -1.5708
    c: Tangent(g1,g2) = 1.5708
    c: Tangent(g1,g3) = -1.5708
    c: Equal(g0,g1)
    c: Vertical(g2)
    c: Diameter(g0) = 6
    c: DistanceY(g1,g0) = 3.4
    c: DistanceX(g-5,g1) = 17.3
    c: DistanceY(g1,g-3) = 3
FEATURE [PartDesign::Pad] Pad186
  BaseFeature = -> Pocket115
  Direction = (0,1,-2e-16)
  Length = 4
  Length2 = 10
  Profile = -> Sketch298
  ReferenceAxis = -> Sketch298 [N_Axis]
  Refine = true
  Suppressed = false
  Type = 0
FEATURE [Sketcher::SketchObject] Sketch299
  ArcFitTolerance = 1e-06
  AttachmentSupport = -> [Pad186]
  ExternalGeometry = -> [Pad186]
  FullyConstrained = true
  MakeInternals = false
  MapMode = 5
  Placement = pos=(0,14.1,-3.5e-15) rot=(0,0.707107,0.707107;3.14159rad)
  sketch-geometry (1):
    g0: Circle CenterX=-14.4 CenterY=-17.6 CenterZ=0 NormalX=0 NormalY=0 NormalZ=1 AngleXU=0 Radius=2.4
  constraints (2):
    c: Coincident(g0,g-3)
    c: Diameter(g0) = 4.8
FEATURE [PartDesign::Pad] Pad187
  BaseFeature = -> Pad186
  Direction = (0,1,-2e-16)
  Length = 2.3
  Length2 = 10
  Profile = -> Sketch299
  ReferenceAxis = -> Sketch299 [N_Axis]
  Refine = true
  Suppressed = false
  Type = 0
FEATURE [Sketcher::SketchObject] Sketch300
  ArcFitTolerance = 1e-06
  AttachmentSupport = -> [Pad187]
  ExternalGeometry = -> [Pad187]
  FullyConstrained = true
  MakeInternals = false
  MapMode = 5
  Placement = pos=(0,16.4,0) rot=(0,0.707107,0.707107;3.14159rad)
  sketch-geometry (1):
    g0: Circle CenterX=-14.4 CenterY=-17.6 CenterZ=0 NormalX=0 NormalY=0 NormalZ=1 AngleXU=0 Radius=0.9
  constraints (2):
    c: Coincident(g0,g-3)
    c: Diameter(g0) = 1.8
FEATURE [PartDesign::Pocket] Pocket116
  BaseFeature = -> Pad187
  Direction = (0,-1,2e-16)
  Length = 5.3
  Length2 = 5
  Profile = -> Sketch300
  ReferenceAxis = -> Sketch300 [N_Axis]
  Refine = true
  Suppressed = false
  Type = 0
FEATURE [Sketcher::SketchObject] Sketch301
  ArcFitTolerance = 1e-06
  AttachmentSupport = -> [Pocket116]
  ExternalGeometry = -> [Pocket116]
  FullyConstrained = true
  MakeInternals = false
  MapMode = 5
  Placement = pos=(0,14.1,-3.5e-15) rot=(0,0.707107,0.707107;3.14159rad)
  sketch-geometry (1):
    g0: Circle CenterX=-14.4 CenterY=-21.9 CenterZ=0 NormalX=0 NormalY=0 NormalZ=1 AngleXU=0 Radius=0.9
  constraints (3):
    c: Diameter(g0) = 1.8
    c: DistanceX(g-3,g0) = 0
    c: DistanceY(g0,g-3) = 0.9
FEATURE [PartDesign::Pocket] Pocket117
  BaseFeature = -> Pocket116
  Direction = (0,-1,2e-16)
  Length = 3
  Length2 = 5
  Profile = -> Sketch301
  ReferenceAxis = -> Sketch301 [N_Axis]
  Refine = true
  Suppressed = false
  Type = 0
FEATURE [Sketcher::SketchObject] Sketch302
  ArcFitTolerance = 1e-06
  AttachmentSupport = -> [Pocket117]
  ExternalGeometry = -> [Pocket117]
  FullyConstrained = true
  MakeInternals = false
  MapMode = 5
  Placement = pos=(0,0,-1e-16) rot=(0,0,1;0rad)
  sketch-geometry (1):
    g0: Circle CenterX=11.75 CenterY=5.05 CenterZ=0 NormalX=0 NormalY=0 NormalZ=1 AngleXU=0 Radius=1.75
  constraints (3):
    c: Diameter(g0) = 3.5
    c: DistanceY(g0,g-4) = 6.05
    c: DistanceX(g-4,g0) = 11.75
FEATURE [PartDesign::Pad] Pad188
  BaseFeature = -> Pocket117
  Direction = (0,0,1)
  Length = 3.7
  Length2 = 10
  Profile = -> Sketch302
  ReferenceAxis = -> Sketch302 [N_Axis]
  Refine = true
  Suppressed = false
  Type = 0
FEATURE [Sketcher::SketchObject] Sketch303
  ArcFitTolerance = 1e-06
  AttachmentOffset = pos=(0,0,-0.75) rot=(0,0,1;0rad)
  AttachmentSupport = -> [Pad188]
  ExternalGeometry = -> [Pad188]
  FullyConstrained = true
  MakeInternals = false
  MapMode = 5
  Placement = pos=(0,13.35,-3.4e-15) rot=(0,0.707107,0.707107;3.14159rad)
  sketch-geometry (4):
    g0: LineSegment StartX=-11.4 StartY=-20.8 StartZ=0 EndX=-10.4 EndY=-20.8 EndZ=0
    g1: ArcOfCircle CenterX=-13.1 CenterY=-20.8 CenterZ=0 NormalX=0 NormalY=0 NormalZ=1 AngleXU=0 Radius=2.7 StartAngle=4.86222 EndAngle=6.28319
    g2: LineSegment StartX=-11.4 StartY=-20.8 StartZ=0 EndX=-11.4 EndY=-21 EndZ=0
    g3: ArcOfCircle CenterX=-14.4 CenterY=-21 CenterZ=0 NormalX=0 NormalY=0 NormalZ=1 AngleXU=0 Radius=2.99999 StartAngle=5.31607 EndAngle=6.28319
  constraints (13):
    c: PointOnObject(g0,g-4)
    c: Horizontal(g0)
    c: Coincident(g1,g0)
    c: PointOnObject(g1,g-3)
    c: DistanceY(g0,g-5) = 2.8
    c: DistanceX(g0,g0) = 1
    c: Radius(g1) = 2.7
    c: DistanceY(g1,g0) = 0
    c: Coincident(g2,g0)
    c: Coincident(g2,g-4)
    c: Coincident(g3,g2)
    c: Coincident(g3,g1)
    c: Tangent(g3,g-3)
FEATURE [PartDesign::Pad] Pad189
  BaseFeature = -> Pad188
  Direction = (0,1,-2e-16)
  Length = 2.5
  Length2 = 10
  Profile = -> Sketch303
  ReferenceAxis = -> Sketch303 [N_Axis]
  Refine = true
  Reversed = true
  Suppressed = false
  Type = 0
FEATURE [PartDesign::Fillet] Fillet011
  Base = -> Pad189 [Edge2,Edge1,Edge16,Edge81,Edge148,Edge90,Edge89,Edge75,Edge150,Edge80,Edge79,Edge88,Edge149,Edge77,Edge78,Edge87,Edge86,Edge61,Edge74]
  BaseFeature = -> Pad189
  Radius = 0.5
  Refine = true
  SupportTransform = false
  Suppressed = false
  UseAllEdges = false
FEATURE [PartDesign::Fillet] Fillet012
  Base = -> Fillet011 [Edge209]
  BaseFeature = -> Fillet011
  Radius = 0.25
  Refine = true
  SupportTransform = false
  Suppressed = false
  UseAllEdges = false
FEATURE [Sketcher::SketchObject] Sketch304
  ArcFitTolerance = 1e-06
  AttachmentSupport = -> [Fillet012]
  ExternalGeometry = -> [Fillet012]
  FullyConstrained = true
  MakeInternals = false
  MapMode = 5
  Placement = pos=(0,9.7,-2.2e-15) rot=(1,0,0;1.5708rad)
  sketch-geometry (4):
    g0: LineSegment StartX=16.95 StartY=-1.5 StartZ=0 EndX=16.95 EndY=-6.5 EndZ=0
    g1: LineSegment StartX=16.95 StartY=-6.5 StartZ=0 EndX=18.95 EndY=-6.5 EndZ=0
    g2: LineSegment StartX=18.95 StartY=-6.5 StartZ=0 EndX=18.95 EndY=-1.5 EndZ=0
    g3: LineSegment StartX=18.95 StartY=-1.5 StartZ=0 EndX=16.95 EndY=-1.5 EndZ=0
  constraints (11):
    c: Coincident(g0,g1)
    c: Coincident(g1,g2)
    c: Coincident(g2,g3)
    c: Coincident(g3,g0)
    c: Vertical(g0)
    c: Vertical(g2)
    c: Horizontal(g1)
    c: Horizontal(g3)
    c: PointOnObject(g1,g-4)
    c: Coincident(g-3,g0)
    c: DistanceY(g2,g2) = 5
FEATURE [PartDesign::Pad] Pad190
  BaseFeature = -> Fillet012
  Direction = (0,-1,2e-16)
  Length = 1
  Length2 = 10
  Profile = -> Sketch304
  ReferenceAxis = -> Sketch304 [N_Axis]
  Refine = true
  Suppressed = false
  Type = 0
FEATURE [PartDesign::Pad] Pad204
  BaseFeature = -> Pad190
  Direction = (0,-2e-16,-1)
  Length = 11.5
  Length2 = 10
  Profile = -> Pad190 [Face51]
  Refine = true
  Suppressed = false
  Type = 0
FEATURE [Sketcher::SketchObject] Sketch318
  ArcFitTolerance = 1e-06
  AttachmentSupport = -> [Pad204]
  ExternalGeometry = -> [Pad204]
  FullyConstrained = true
  MakeInternals = false
  MapMode = 5
  Placement = pos=(0,0,-18) rot=(1,0,0;3.14159rad)
  sketch-geometry (4):
    g0: LineSegment StartX=16.95 StartY=-3 StartZ=0 EndX=16.95 EndY=-3.1 EndZ=0
    g1: LineSegment StartX=16.95 StartY=-3.1 StartZ=0 EndX=18.95 EndY=-3.1 EndZ=0
    g2: LineSegment StartX=18.95 StartY=-3.1 StartZ=0 EndX=18.95 EndY=-3 EndZ=0
    g3: LineSegment StartX=18.95 StartY=-3 StartZ=0 EndX=16.95 EndY=-3 EndZ=0
  constraints (10):
    c: Coincident(g0,g1)
    c: Coincident(g1,g2)
    c: Coincident(g2,g3)
    c: Coincident(g3,g0)
    c: Vertical(g0)
    c: Vertical(g2)
    c: Horizontal(g1)
    c: Coincident(g0,g-3)
    c: DistanceY(g0,g0) = 0.1
    c: Coincident(g2,g-3)
FEATURE [PartDesign::Body] Body011  label="Left_Foot"
  AllowCompound = false
  Group = -> [Sketch285,Pad174,Sketch286,Pad175,Sketch287,Pad176,Sketch288,Pad177,Sketch289,Pad178,Sketch290,Pad179,Sketch291,Pad180,Sketch292,Pad181,Sketch293,Pad182,Sketch294,Pocket114,Sketch295,Pad183,Sketch296,Pad184,Pad185,Sketch297,Pocket115,Sketch298,Pad186,Sketch299,Pad187,Sketch300,Pocket116,Sketch301,Pocket117,Sketch302,Pad188,Sketch303,Pad189,Fillet011,Fillet012,Sketch304,Pad190,Pad204,Sketch318,+9 more]
  Origin = -> Origin011
  Placement = pos=(-67.75,1.4e-15,11.5) rot=(0,0,1;0rad)
  Tip = -> Pad245
COMPONENT P7 — recipe-attached ("Scoop_Rod", modeled in this document).
Construction recipe (the document's own serialized feature program — sketch geometry with constraints, then the solid features built on it; lengths are millimeters unless a unit is written):

FEATURE [PartDesign::SubShapeBinder] Binder003
  BindCopyOnChange = 0
  BindMode = 2
  ClaimChildren = false
  Context = -> Body014 [Binder003.]
  Fuse = false
  MakeFace = true
  OffsetFill = false
  OffsetIntersection = false
  OffsetJoinType = 0
  OffsetOpenResult = false
  PartialLoad = false
  Refine = true
  Relative = true
  _Version = 2
FEATURE [Sketcher::SketchObject] Sketch314
  ArcFitTolerance = 1e-06
  AttachmentSupport = -> [Binder003]
  ExternalGeometry = -> [Binder003]
  FullyConstrained = true
  MakeInternals = false
  MapMode = 5
  Placement = pos=(0,-8.05,0) rot=(0,0.707107,0.707107;3.14159rad)
  sketch-geometry (6):
    g0: ArcOfCircle CenterX=9.72007 CenterY=7.50503 CenterZ=0 NormalX=0 NormalY=0 NormalZ=1 AngleXU=0 Radius=0.3 StartAngle=0.535959 EndAngle=2.50091
    g1: LineSegment [constr] StartX=9.71746 StartY=7.4551 StartZ=0 EndX=9.73316 EndY=7.75469 EndZ=0
    g2: LineSegment [constr] StartX=9.73316 StartY=7.75469 StartZ=0 EndX=9.47648 EndY=7.63379 EndZ=0
    g3: LineSegment [constr] StartX=9.73316 StartY=7.75469 StartZ=0 EndX=9.97579 EndY=7.60762 EndZ=0
    g4: LineSegment [constr] StartX=9.73656 StartY=7.80458 StartZ=0 EndX=9.72007 EndY=7.50503 EndZ=0
    g5: ArcOfCircle CenterX=9.80354 CenterY=9.0977 CenterZ=0 NormalX=0 NormalY=0 NormalZ=1 AngleXU=0 Radius=1.45 StartAngle=4.833 EndAngle=10.7702
  constraints (19):
    c: Radius(g0) = 0.3
    c: Coincident(g1,g-5)
    c: PointOnObject(g1,g-5)
    c: Coincident(g2,g1)
    c: Coincident(g2,g-5)
    c: Coincident(g3,g1)
    c: Coincident(g3,g-5)
    c: Distance(g2) = 0.283727
    c: Distance(g3) = 0.283728
    c: PointOnObject(g4,g0)
    c: Coincident(g4,g0)
    c: PointOnObject(g0,g1)
    c: Distance(g0,g4) = 0.283727
    c: Distance(g0,g1) = 0.05
    c: Coincident(g5,g0)
    c: Coincident(g5,g0)
    c: Coincident(g5,g-4)
    c: Diameter(g-3) = 3
    c: Diameter(g5) = 2.9
FEATURE [PartDesign::Pad] Pad199
  Direction = (0,1,-2e-16)
  Length = 17.5
  Length2 = 10
  Profile = -> Sketch314
  ReferenceAxis = -> Sketch314 [N_Axis]
  Refine = true
  Suppressed = false
  Type = 0
FEATURE [PartDesign::Pad] Pad200
  BaseFeature = -> Pad199
  Direction = (0,1,-2e-16)
  Length = 1.4
  Length2 = 10
  Profile = -> Sketch314
  ReferenceAxis = -> Sketch314 [N_Axis]
  Refine = true
  Reversed = true
  Suppressed = false
  Type = 0
FEATURE [Sketcher::SketchObject] Sketch315
  ArcFitTolerance = 1e-06
  AttachmentOffset = pos=(0,0,-1.3) rot=(0,0,1;0rad)
  AttachmentSupport = -> [Pad200]
  ExternalGeometry = -> [Pad200]
  FullyConstrained = true
  MakeInternals = false
  MapMode = 5
  Placement = pos=(0,-8.15,-3e-16) rot=(1,0,0;1.5708rad)
  sketch-geometry (2):
    g0: ArcOfCircle CenterX=-9.72007 CenterY=7.50503 CenterZ=0 NormalX=0 NormalY=0 NormalZ=1 AngleXU=0 Radius=0.3 StartAngle=0.640679 EndAngle=2.60563
    g1: ArcOfCircle CenterX=-9.80354 CenterY=9.0977 CenterZ=0 NormalX=0 NormalY=0 NormalZ=1 AngleXU=0 Radius=1.45 StartAngle=4.59178 EndAngle=4.93772
  constraints (6):
    c: Coincident(g0,g-4)
    c: Coincident(g0,g-4)
    c: Tangent(g0,g-3)
    c: Coincident(g1,g0)
    c: Coincident(g1,g0)
    c: Diameter(g1) = 2.9
FEATURE [PartDesign::Pad] Pad201
  BaseFeature = -> Pad200
  Direction = (0,-1,2e-16)
  Length = 0.3
  Length2 = 10
  Profile = -> Sketch315
  ReferenceAxis = -> Sketch315 [N_Axis]
  Refine = true
  Suppressed = false
  Type = 0
FEATURE [Sketcher::SketchObject] Sketch316
  ArcFitTolerance = 1e-06
  AttachmentOffset = pos=(0,0,-1.3) rot=(0,0,1;0rad)
  AttachmentSupport = -> [Pad201]
  ExternalGeometry = -> [Pad201]
  FullyConstrained = true
  MakeInternals = false
  MapMode = 5
  Placement = pos=(0,8.15,3e-16) rot=(0,0.707107,0.707107;3.14159rad)
  sketch-geometry (2):
    g0: ArcOfCircle CenterX=9.72007 CenterY=7.50503 CenterZ=0 NormalX=0 NormalY=0 NormalZ=1 AngleXU=0 Radius=0.3 StartAngle=0.535959 EndAngle=2.50091
    g1: ArcOfCircle CenterX=9.80354 CenterY=9.0977 CenterZ=0 NormalX=0 NormalY=0 NormalZ=1 AngleXU=0 Radius=1.45 StartAngle=4.48706 EndAngle=4.833
  constraints (6):
    c: Coincident(g0,g-4)
    c: Coincident(g0,g-4)
    c: Tangent(g0,g-3)
    c: Coincident(g1,g0)
    c: Coincident(g1,g0)
    c: Diameter(g1) = 2.9
FEATURE [PartDesign::Pad] Pad202
  BaseFeature = -> Pad201
  Direction = (0,1,-2e-16)
  Length = 0.3
  Length2 = 10
  Profile = -> Sketch316
  ReferenceAxis = -> Sketch316 [N_Axis]
  Refine = true
  Suppressed = false
  Type = 0
FEATURE [PartDesign::Body] Body014  label="Scoop_Rod"
  AllowCompound = false
  Group = -> [Binder003,Sketch314,Pad199,Pad200,Sketch315,Pad201,Sketch316,Pad202]
  Origin = -> Origin014
  Tip = -> Pad202
COMPONENT P8 — recipe-attached ("Pre_Right_Foot", modeled in this document).
Construction recipe (the document's own serialized feature program — sketch geometry with constraints, then the solid features built on it; lengths are millimeters unless a unit is written):

FEATURE [Sketcher::SketchObject] Sketch319
  ArcFitTolerance = 1e-06
  AttachmentSupport = -> [XY_Plane015]
  FullyConstrained = true
  MakeInternals = false
  MapMode = 5
  sketch-geometry (4):
    g0: LineSegment StartX=0 StartY=0 StartZ=0 EndX=31.7 EndY=0 EndZ=0
    g1: LineSegment StartX=31.7 StartY=0 StartZ=0 EndX=31.7 EndY=11.1 EndZ=0
    g2: LineSegment StartX=31.7 StartY=11.1 StartZ=0 EndX=0 EndY=11.1 EndZ=0
    g3: LineSegment StartX=0 StartY=11.1 StartZ=0 EndX=0 EndY=0 EndZ=0
  constraints (11):
    c: Coincident(g0,g1)
    c: Coincident(g1,g2)
    c: Coincident(g2,g3)
    c: Coincident(g3,g0)
    c: Horizontal(g0)
    c: Horizontal(g2)
    c: Vertical(g1)
    c: Vertical(g3)
    c: Coincident(g0,g-1)
    c: DistanceY(g1,g1) = 11.1
    c: DistanceX(g2,g2) = 31.7
FEATURE [PartDesign::Pad] Pad207
  Direction = (0,0,1)
  Length = 1.5
  Length2 = 10
  Profile = -> Sketch319
  ReferenceAxis = -> Sketch319 [N_Axis]
  Refine = true
  Reversed = true
  Suppressed = false
  Type = 0
FEATURE [Sketcher::SketchObject] Sketch320
  ArcFitTolerance = 1e-06
  AttachmentSupport = -> [Pad207]
  ExternalGeometry = -> [Pad207]
  FullyConstrained = true
  MakeInternals = false
  MapMode = 5
  Placement = pos=(0,0,0) rot=(1,0,0;1.5708rad)
  sketch-geometry (10):
    g0: LineSegment StartX=0 StartY=-1.5 StartZ=0 EndX=0 EndY=-14.5 EndZ=0
    g1: LineSegment StartX=0 StartY=-14.5 StartZ=0 EndX=-2.1 EndY=-14.5 EndZ=0
    g2: LineSegment StartX=-2.1 StartY=-14.5 StartZ=0 EndX=-2.1 EndY=-18 EndZ=0
    g3: LineSegment StartX=-2.1 StartY=-18 StartZ=0 EndX=18.95 EndY=-18 EndZ=0
    g4: LineSegment StartX=18.95 StartY=-18 StartZ=0 EndX=18.95 EndY=-7.5 EndZ=0
    g5: LineSegment StartX=18.95 StartY=-7.5 StartZ=0 EndX=30.2 EndY=-7.5 EndZ=0
    g6: LineSegment StartX=30.2 StartY=-7.5 StartZ=0 EndX=30.2 EndY=-8 EndZ=0
    g7: LineSegment StartX=30.2 StartY=-8 StartZ=0 EndX=31.7 EndY=-8 EndZ=0
    g8: LineSegment StartX=31.7 StartY=-8 StartZ=0 EndX=31.7 EndY=-1.5 EndZ=0
    g9: LineSegment StartX=0 StartY=-1.5 StartZ=0 EndX=31.7 EndY=-1.5 EndZ=0
  constraints (28):
    c: Coincident(g0,g-3)
    c: PointOnObject(g0,g-2)
    c: Coincident(g1,g0)
    c: Horizontal(g1)
    c: Coincident(g2,g1)
    c: Coincident(g3,g2)
    c: Horizontal(g3)
    c: Coincident(g4,g3)
    c: Vertical(g4)
    c: Coincident(g5,g4)
    c: Horizontal(g5)
    c: Coincident(g6,g5)
    c: Vertical(g6)
    c: Coincident(g7,g6)
    c: Horizontal(g7)
    c: Coincident(g8,g7)
    c: Coincident(g8,g-3)
    c: Vertical(g8)
    c: DistanceY(g2,g0) = 16.5
    c: Vertical(g2)
    c: DistanceY(g2,g2) = 3.5
    c: DistanceY(g4,g4) = 10.5
    c: DistanceX(g4,g7) = 12.75
    c: DistanceY(g6,g6) = 0.5
    c: DistanceX(g7,g7) = 1.5
    c: Coincident(g9,g0)
    c: Coincident(g9,g8)
    c: DistanceX(g1,g1) = 2.1
FEATURE [PartDesign::Pad] Pad208
  BaseFeature = -> Pad207
  Direction = (0,-1,2e-16)
  Length = 1.75
  Length2 = 10
  Profile = -> Sketch320
  ReferenceAxis = -> Sketch320 [N_Axis]
  Refine = true
  Reversed = true
  Suppressed = false
  Type = 0
FEATURE [Sketcher::SketchObject] Sketch321
  ArcFitTolerance = 1e-06
  AttachmentSupport = -> [Pad208]
  ExternalGeometry = -> [Pad208]
  FullyConstrained = true
  MakeInternals = false
  MapMode = 5
  Placement = pos=(0,1.75,-4e-16) rot=(0,0.707107,0.707107;3.14159rad)
  sketch-geometry (4):
    g0: LineSegment StartX=-18.95 StartY=-18 StartZ=0 EndX=-16.95 EndY=-18 EndZ=0
    g1: LineSegment StartX=-16.95 StartY=-18 StartZ=0 EndX=-16.95 EndY=-1.5 EndZ=0
    g2: LineSegment StartX=-16.95 StartY=-1.5 StartZ=0 EndX=-18.95 EndY=-1.5 EndZ=0
    g3: LineSegment StartX=-18.95 StartY=-1.5 StartZ=0 EndX=-18.95 EndY=-18 EndZ=0
  constraints (11):
    c: Coincident(g0,g1)
    c: Coincident(g1,g2)
    c: Coincident(g2,g3)
    c: Coincident(g3,g0)
    c: Horizontal(g0)
    c: Horizontal(g2)
    c: Vertical(g1)
    c: Vertical(g3)
    c: Coincident(g0,g-4)
    c: PointOnObject(g1,g-5)
    c: DistanceX(g0,g0) = 2
FEATURE [PartDesign::Pad] Pad209
  BaseFeature = -> Pad208
  Direction = (0,1,-2e-16)
  Length = 1.25
  Length2 = 10
  Profile = -> Sketch321
  ReferenceAxis = -> Sketch321 [N_Axis]
  Refine = true
  Suppressed = false
  Type = 0
FEATURE [Sketcher::SketchObject] Sketch322
  ArcFitTolerance = 1e-06
  AttachmentSupport = -> [Pad209]
  ExternalGeometry = -> [Pad209]
  FullyConstrained = true
  MakeInternals = false
  MapMode = 5
  Placement = pos=(0,11.1,0) rot=(0,0.707107,0.707107;3.14159rad)
  sketch-geometry (5):
    g0: LineSegment StartX=-31.7 StartY=-1.5 StartZ=0 EndX=0 EndY=-1.5 EndZ=0
    g1: LineSegment StartX=0 StartY=-1.5 StartZ=0 EndX=0 EndY=-18 EndZ=0
    g2: LineSegment StartX=0 StartY=-18 StartZ=0 EndX=-27.2 EndY=-18 EndZ=0
    g3: LineSegment StartX=-27.2 StartY=-18 StartZ=0 EndX=-31.7 EndY=-21 EndZ=0
    g4: LineSegment StartX=-31.7 StartY=-1.5 StartZ=0 EndX=-31.7 EndY=-21 EndZ=0
  constraints (13):
    c: Coincident(g0,g-3)
    c: Coincident(g0,g-3)
    c: Coincident(g1,g0)
    c: PointOnObject(g1,g-4)
    c: Vertical(g1)
    c: Coincident(g2,g1)
    c: Horizontal(g2)
    c: Coincident(g3,g2)
    c: Coincident(g4,g0)
    c: Coincident(g4,g3)
    c: Vertical(g4)
    c: DistanceX(g3,g2) = 4.5
    c: DistanceY(g3,g2) = 3
FEATURE [PartDesign::Pad] Pad210
  BaseFeature = -> Pad209
  Direction = (0,1,-2e-16)
  Length = 1.4
  Length2 = 10
  Profile = -> Sketch322
  ReferenceAxis = -> Sketch322 [N_Axis]
  Refine = true
  Reversed = true
  Suppressed = false
  Type = 0
FEATURE [Sketcher::SketchObject] Sketch323
  ArcFitTolerance = 1e-06
  AttachmentSupport = -> [Pad210]
  ExternalGeometry = -> [Pad210]
  FullyConstrained = true
  MakeInternals = false
  MapMode = 5
  Placement = pos=(31.7,0,0) rot=(0.57735,0.57735,0.57735;2.0944rad)
  sketch-geometry (4):
    g0: LineSegment StartX=1.75 StartY=-1.5 StartZ=0 EndX=1.75 EndY=-8 EndZ=0
    g1: LineSegment StartX=1.75 StartY=-8 StartZ=0 EndX=9.7 EndY=-8 EndZ=0
    g2: LineSegment StartX=9.7 StartY=-8 StartZ=0 EndX=9.7 EndY=-1.5 EndZ=0
    g3: LineSegment StartX=9.7 StartY=-1.5 StartZ=0 EndX=1.75 EndY=-1.5 EndZ=0
  constraints (10):
    c: Coincident(g0,g1)
    c: Coincident(g1,g2)
    c: Coincident(g2,g3)
    c: Coincident(g3,g0)
    c: Vertical(g2)
    c: Horizontal(g1)
    c: Horizontal(g3)
    c: Coincident(g0,g-5)
    c: PointOnObject(g1,g-4)
    c: Coincident(g0,g-5)
FEATURE [PartDesign::Pad] Pad211
  BaseFeature = -> Pad210
  Direction = (1,0,0)
  Length = 1.5
  Length2 = 10
  Profile = -> Sketch323
  ReferenceAxis = -> Sketch323 [N_Axis]
  Refine = true
  Reversed = true
  Suppressed = false
  Type = 0
FEATURE [Sketcher::SketchObject] Sketch324
  ArcFitTolerance = 1e-06
  AttachmentSupport = -> [Pad211]
  ExternalGeometry = -> [Pad211]
  FullyConstrained = true
  MakeInternals = false
  MapMode = 5
  Placement = pos=(0,0,0) rot=(0.57735,-0.57735,-0.57735;2.0944rad)
  sketch-geometry (6):
    g0: LineSegment StartX=-9.7 StartY=-1.5 StartZ=0 EndX=-9.7 EndY=-18 EndZ=0
    g1: LineSegment StartX=-1.75 StartY=-7.5 StartZ=0 EndX=-1.75 EndY=-1.5 EndZ=0
    g2: LineSegment StartX=-1.75 StartY=-1.5 StartZ=0 EndX=-9.7 EndY=-1.5 EndZ=0
    g3: LineSegment StartX=-9.7 StartY=-18 StartZ=0 EndX=-6.6 EndY=-18 EndZ=0
    g4: LineSegment StartX=-6.6 StartY=-18 StartZ=0 EndX=-6.6 EndY=-7.5 EndZ=0
    g5: LineSegment StartX=-1.75 StartY=-7.5 StartZ=0 EndX=-6.6 EndY=-7.5 EndZ=0
  constraints (17):
    c: Coincident(g1,g2)
    c: Coincident(g2,g0)
    c: Vertical(g1)
    c: Horizontal(g2)
    c: Coincident(g0,g-5)
    c: PointOnObject(g1,g-3)
    c: Coincident(g0,g-5)
    c: Coincident(g3,g0)
    c: Horizontal(g3)
    c: Coincident(g4,g3)
    c: Vertical(g4)
    c: DistanceY(g1,g1) = 6
    c: Coincident(g5,g1)
    c: Coincident(g5,g4)
    c: Horizontal(g5)
    c: DistanceX(g3,g3) = 3.1
    c: DistanceX(g-6,g-6) = 1.4
FEATURE [PartDesign::Pad] Pad212
  BaseFeature = -> Pad211
  Direction = (-1,0,0)
  Length = 1.5
  Length2 = 10
  Profile = -> Sketch324
  ReferenceAxis = -> Sketch324 [N_Axis]
  Refine = true
  Reversed = true
  Suppressed = false
  Type = 0
FEATURE [Sketcher::SketchObject] Sketch325
  ArcFitTolerance = 1e-06
  AttachmentSupport = -> [Pad212]
  ExternalGeometry = -> [Pad212]
  FullyConstrained = true
  MakeInternals = false
  MapMode = 5
  Placement = pos=(0,0,0) rot=(0.57735,-0.57735,-0.57735;2.0944rad)
  sketch-geometry (4):
    g0: LineSegment StartX=-6.6 StartY=-18 StartZ=0 EndX=-6.6 EndY=-14.5 EndZ=0
    g1: LineSegment StartX=-6.6 StartY=-14.5 StartZ=0 EndX=-11.1 EndY=-14.5 EndZ=0
    g2: LineSegment StartX=-11.1 StartY=-14.5 StartZ=0 EndX=-11.1 EndY=-18 EndZ=0
    g3: LineSegment StartX=-11.1 StartY=-18 StartZ=0 EndX=-6.6 EndY=-18 EndZ=0
  constraints (12):
    c: Coincident(g0,g1)
    c: Coincident(g1,g2)
    c: Coincident(g2,g3)
    c: Coincident(g3,g0)
    c: Vertical(g0)
    c: Vertical(g2)
    c: Horizontal(g1)
    c: Horizontal(g3)
    c: Coincident(g0,g-4)
    c: PointOnObject(g1,g-5)
    c: DistanceY(g-6,g-6) = 3.5
    c: DistanceY(g0,g0) = 3.5
FEATURE [PartDesign::Pad] Pad213
  BaseFeature = -> Pad212
  Direction = (-1,0,0)
  Length = 2.1
  Length2 = 10
  Profile = -> Sketch325
  ReferenceAxis = -> Sketch325 [N_Axis]
  Refine = true
  Suppressed = false
  Type = 0
FEATURE [Sketcher::SketchObject] Sketch326
  ArcFitTolerance = 1e-06
  AttachmentSupport = -> [Pad213]
  ExternalGeometry = -> [Pad213]
  FullyConstrained = true
  MakeInternals = false
  MapMode = 5
  Placement = pos=(0,0,-18) rot=(1,0,0;3.14159rad)
  sketch-geometry (6):
    g0: LineSegment StartX=-1.25 StartY=-14.8 StartZ=0 EndX=2.95 EndY=-14.8 EndZ=0
    g1: LineSegment StartX=3.8 StartY=-11.1 StartZ=0 EndX=-2.1 EndY=-11.1 EndZ=0
    g2: LineSegment StartX=-2.1 StartY=-11.1 StartZ=0 EndX=-2.1 EndY=-12.6 EndZ=0
    g3: LineSegment StartX=-2.1 StartY=-12.6 StartZ=0 EndX=-1.25 EndY=-14.8 EndZ=0
    g4: LineSegment StartX=2.95 StartY=-14.8 StartZ=0 EndX=3.8 EndY=-12.6 EndZ=0
    g5: LineSegment StartX=3.8 StartY=-12.6 StartZ=0 EndX=3.8 EndY=-11.1 EndZ=0
  constraints (17):
    c: Horizontal(g0)
    c: Coincident(g2,g1)
    c: Vertical(g2)
    c: Coincident(g3,g2)
    c: Coincident(g3,g0)
    c: Coincident(g4,g0)
    c: Coincident(g5,g4)
    c: PointOnObject(g5,g-3)
    c: Vertical(g5)
    c: Coincident(g1,g5)
    c: DistanceX(g1,g1) = 5.9
    c: DistanceX(g0,g0) = 4.2
    c: DistanceY(g0,g1) = 3.7
    c: Coincident(g1,g-3)
    c: DistanceY(g2,g2) = 1.5
    c: DistanceY(g5,g5) = 1.5
    c: DistanceX(g2,g0) = 0.85
FEATURE [PartDesign::Pad] Pad214
  BaseFeature = -> Pad213
  Direction = (0,0,-1)
  Length = 3.5
  Length2 = 10
  Profile = -> Sketch326
  ReferenceAxis = -> Sketch326 [N_Axis]
  Refine = true
  Reversed = true
  Suppressed = false
  Type = 0
FEATURE [Sketcher::SketchObject] Sketch327
  ArcFitTolerance = 1e-06
  AttachmentSupport = -> [Pad214]
  ExternalGeometry = -> [Pad214]
  FullyConstrained = true
  MakeInternals = false
  MapMode = 5
  Placement = pos=(0,11.1,0) rot=(0,0.707107,0.707107;3.14159rad)
  sketch-geometry (1):
    g0: Circle CenterX=-6.15 CenterY=-11.45 CenterZ=0 NormalX=0 NormalY=0 NormalZ=1 AngleXU=0 Radius=1.95
  constraints (3):
    c: Diameter(g0) = 3.9
    c: DistanceX(g0,g-1) = 6.15
    c: DistanceY(g-4,g0) = 6.55
FEATURE [PartDesign::Pad] Pad215
  BaseFeature = -> Pad214
  Direction = (0,1,-2e-16)
  Length = 3.1
  Length2 = 10
  Profile = -> Sketch327
  ReferenceAxis = -> Sketch327 [N_Axis]
  Refine = true
  Suppressed = false
  Type = 0
FEATURE [Sketcher::SketchObject] Sketch328
  ArcFitTolerance = 1e-06
  AttachmentSupport = -> [Pad215]
  ExternalGeometry = -> [Pad215]
  FullyConstrained = true
  MakeInternals = false
  MapMode = 5
  Placement = pos=(4.3e-15,14.2,-7.5e-15) rot=(0,0.707107,0.707107;3.14159rad)
  sketch-geometry (1):
    g0: Circle CenterX=-6.15 CenterY=-11.45 CenterZ=0 NormalX=0 NormalY=0 NormalZ=1 AngleXU=0 Radius=0.9
  constraints (2):
    c: Coincident(g0,g-3)
    c: Diameter(g0) = 1.8
FEATURE [PartDesign::Pocket] Pocket121
  BaseFeature = -> Pad215
  Direction = (0,-1,2e-16)
  Length = 16
  Length2 = 5
  Profile = -> Sketch328
  ReferenceAxis = -> Sketch328 [N_Axis]
  Refine = true
  Suppressed = false
  Type = 0
FEATURE [Sketcher::SketchObject] Sketch329
  ArcFitTolerance = 1e-06
  AttachmentSupport = -> [Pocket121]
  ExternalGeometry = -> [Pocket121]
  FullyConstrained = true
  MakeInternals = false
  MapMode = 5
  Placement = pos=(0,11.1,0) rot=(0,0.707107,0.707107;3.14159rad)
  sketch-geometry (4):
    g0: LineSegment StartX=-7.6 StartY=-10.1462 StartZ=0 EndX=-7.6 EndY=-4.49617 EndZ=0
    g1: LineSegment StartX=-4.7 StartY=-10.1462 StartZ=0 EndX=-4.7 EndY=-4.49616 EndZ=0
    g2: ArcOfCircle CenterX=-6.15 CenterY=-4.49616 CenterZ=0 NormalX=0 NormalY=0 NormalZ=1 AngleXU=0 Radius=1.45 StartAngle=0 EndAngle=3.1416
    g3: ArcOfCircle CenterX=-6.15 CenterY=-11.45 CenterZ=0 NormalX=0 NormalY=0 NormalZ=1 AngleXU=0 Radius=1.95 StartAngle=0.732373 EndAngle=2.40922
  constraints (13):
    c: PointOnObject(g0,g-3)
    c: Vertical(g0)
    c: Vertical(g1)
    c: Coincident(g2,g0)
    c: Coincident(g2,g1)
    c: Diameter(g2) = 2.9
    c: Coincident(g3,g0)
    c: Coincident(g3,g1)
    c: Coincident(g3,g-3)
    c: DistanceX(g0,g3) = 1.45
    c: DistanceX(g3,g1) = 1.45
    c: DistanceY(g1,g2) = 0
    c: DistanceY(g1,g2) = 5.65
FEATURE [PartDesign::Pad] Pad216
  BaseFeature = -> Pocket121
  Direction = (0,1,-2e-16)
  Length = 2
  Length2 = 10
  Profile = -> Sketch329
  ReferenceAxis = -> Sketch329 [N_Axis]
  Refine = true
  Suppressed = false
  Type = 0
FEATURE [Sketcher::SketchObject] Sketch330
  ArcFitTolerance = 1e-06
  AttachmentSupport = -> [Pad216]
  ExternalGeometry = -> [Pad216]
  FullyConstrained = true
  MakeInternals = false
  MapMode = 5
  Placement = pos=(0,11.1,0) rot=(0,0.707107,0.707107;3.14159rad)
  sketch-geometry (8):
    g0: LineSegment StartX=-31.7 StartY=-7.55 StartZ=0 EndX=-31.7 EndY=1.5 EndZ=0
    g1: ArcOfCircle CenterX=-31.7 CenterY=0 CenterZ=0 NormalX=0 NormalY=0 NormalZ=1 AngleXU=0 Radius=1.5 StartAngle=0 EndAngle=1.5708
    g2: LineSegment StartX=-30.2 StartY=0 StartZ=0 EndX=-24 EndY=0 EndZ=0
    g3: ArcOfCircle CenterX=-24 CenterY=-1 CenterZ=0 NormalX=0 NormalY=0 NormalZ=1 AngleXU=0 Radius=1 StartAngle=4.71239 EndAngle=7.85398
    g4: LineSegment StartX=-24 StartY=-2 StartZ=0 EndX=-26.3 EndY=-2 EndZ=0
    g5: LineSegment StartX=-26.3 StartY=-2 StartZ=0 EndX=-30.2 EndY=-5.9 EndZ=0
    g6: LineSegment StartX=-30.2 StartY=-5.9 StartZ=0 EndX=-30.2 EndY=-7.55 EndZ=0
    g7: ArcOfCircle CenterX=-30.95 CenterY=-7.55 CenterZ=0 NormalX=0 NormalY=0 NormalZ=1 AngleXU=0 Radius=0.75 StartAngle=3.14159 EndAngle=6.28319
  constraints (26):
    c: PointOnObject(g0,g-3)
    c: Vertical(g0)
    c: Coincident(g1,g0)
    c: PointOnObject(g1,g-4)
    c: Coincident(g2,g1)
    c: PointOnObject(g2,g-4)
    c: Coincident(g3,g2)
    c: Coincident(g4,g3)
    c: Horizontal(g4)
    c: Coincident(g5,g4)
    c: Coincident(g6,g5)
    c: Coincident(g7,g0)
    c: Coincident(g7,g6)
    c: Diameter(g7) = 1.5
    c: Radius(g1) = 1.5
    c: Diameter(g3) = 2
    c: Angle(g5,g4) = 2.35619
    c: Vertical(g6)
    c: Coincident(g1,g-4)
    c: DistanceX(g0,g2) = 7.7
    c: DistanceX(g2,g3) = 0
    c: DistanceX(g3,g3) = 0
    c: DistanceY(g0,g0) = 9.05
    c: DistanceY(g6,g7) = 0
    c: DistanceY(g0,g7) = 0
    c: DistanceX(g4,g3) = 2.3
FEATURE [PartDesign::Pad] Pad217
  BaseFeature = -> Pad216
  Direction = (0,1,-2e-16)
  Length = 5
  Length2 = 10
  Profile = -> Sketch330
  ReferenceAxis = -> Sketch330 [N_Axis]
  Refine = true
  Suppressed = false
  Type = 0
FEATURE [PartDesign::Pad] Pad218
  BaseFeature = -> Pad217
  Direction = (0,-1,0)
  Length = 4.8
  Length2 = 10
  Profile = -> Pad217 [Face1]
  Refine = true
  Suppressed = false
  Type = 0
FEATURE [Sketcher::SketchObject] Sketch331
  ArcFitTolerance = 1e-06
  AttachmentSupport = -> [Pad218]
  ExternalGeometry = -> [Pad218]
  FullyConstrained = true
  MakeInternals = false
  MapMode = 5
  Placement = pos=(0,0,0) rot=(1,0,0;1.5708rad)
  sketch-geometry (1):
    g0: Circle CenterX=6.15 CenterY=-11.45 CenterZ=0 NormalX=0 NormalY=0 NormalZ=1 AngleXU=0 Radius=2.7
  constraints (2):
    c: Coincident(g0,g-3)
    c: Diameter(g0) = 5.4
FEATURE [PartDesign::Pocket] Pocket122
  BaseFeature = -> Pad218
  Direction = (0,1,-2e-16)
  Length = 0.5
  Length2 = 5
  Profile = -> Sketch331
  ReferenceAxis = -> Sketch331 [N_Axis]
  Refine = true
  Suppressed = false
  Type = 0
FEATURE [Sketcher::SketchObject] Sketch332
  ArcFitTolerance = 1e-06
  AttachmentOffset = pos=(0,0,-1) rot=(0,0,1;0rad)
  AttachmentSupport = -> [Pocket122]
  ExternalGeometry = -> [Pocket122]
  FullyConstrained = true
  MakeInternals = false
  MapMode = 5
  Placement = pos=(0,10.1,2e-16) rot=(0,0.707107,0.707107;3.14159rad)
  sketch-geometry (4):
    g0: ArcOfCircle CenterX=-14.4 CenterY=-17.6 CenterZ=0 NormalX=0 NormalY=0 NormalZ=1 AngleXU=0 Radius=3 StartAngle=5e-16 EndAngle=3.14159
    g1: ArcOfCircle CenterX=-14.4 CenterY=-21 CenterZ=0 NormalX=0 NormalY=0 NormalZ=1 AngleXU=0 Radius=3 StartAngle=3.14159 EndAngle=6.28319
    g2: LineSegment StartX=-11.4 StartY=-17.6 StartZ=0 EndX=-11.4 EndY=-21 EndZ=0
    g3: LineSegment StartX=-17.4 StartY=-17.6 StartZ=0 EndX=-17.4 EndY=-21 EndZ=0
  constraints (10):
    c: Tangent(g0,g2) = 1.5708
    c: Tangent(g0,g3) = -1.5708
    c: Tangent(g1,g2) = 1.5708
    c: Tangent(g1,g3) = -1.5708
    c: Equal(g0,g1)
    c: Vertical(g2)
    c: Diameter(g0) = 6
    c: DistanceY(g1,g0) = 3.4
    c: DistanceX(g-5,g1) = 17.3
    c: DistanceY(g1,g-3) = 3
FEATURE [PartDesign::Pad] Pad219
  BaseFeature = -> Pocket122
  Direction = (0,1,-2e-16)
  Length = 4
  Length2 = 10
  Profile = -> Sketch332
  ReferenceAxis = -> Sketch332 [N_Axis]
  Refine = true
  Suppressed = false
  Type = 0
FEATURE [Sketcher::SketchObject] Sketch333
  ArcFitTolerance = 1e-06
  AttachmentSupport = -> [Pad219]
  ExternalGeometry = -> [Pad219]
  FullyConstrained = true
  MakeInternals = false
  MapMode = 5
  Placement = pos=(0,14.1,-3.5e-15) rot=(0,0.707107,0.707107;3.14159rad)
  sketch-geometry (1):
    g0: Circle CenterX=-14.4 CenterY=-17.6 CenterZ=0 NormalX=0 NormalY=0 NormalZ=1 AngleXU=0 Radius=2.4
  constraints (2):
    c: Coincident(g0,g-3)
    c: Diameter(g0) = 4.8
FEATURE [PartDesign::Pad] Pad220
  BaseFeature = -> Pad219
  Direction = (0,1,-2e-16)
  Length = 2.3
  Length2 = 10
  Profile = -> Sketch333
  ReferenceAxis = -> Sketch333 [N_Axis]
  Refine = true
  Suppressed = false
  Type = 0
FEATURE [Sketcher::SketchObject] Sketch334
  ArcFitTolerance = 1e-06
  AttachmentSupport = -> [Pad220]
  ExternalGeometry = -> [Pad220]
  FullyConstrained = true
  MakeInternals = false
  MapMode = 5
  Placement = pos=(0,16.4,0) rot=(0,0.707107,0.707107;3.14159rad)
  sketch-geometry (1):
    g0: Circle CenterX=-14.4 CenterY=-17.6 CenterZ=0 NormalX=0 NormalY=0 NormalZ=1 AngleXU=0 Radius=0.9
  constraints (2):
    c: Coincident(g0,g-3)
    c: Diameter(g0) = 1.8
FEATURE [PartDesign::Pocket] Pocket123
  BaseFeature = -> Pad220
  Direction = (0,-1,2e-16)
  Length = 5.3
  Length2 = 5
  Profile = -> Sketch334
  ReferenceAxis = -> Sketch334 [N_Axis]
  Refine = true
  Suppressed = false
  Type = 0
FEATURE [Sketcher::SketchObject] Sketch335
  ArcFitTolerance = 1e-06
  AttachmentSupport = -> [Pocket123]
  ExternalGeometry = -> [Pocket123]
  FullyConstrained = true
  MakeInternals = false
  MapMode = 5
  Placement = pos=(0,14.1,-3.5e-15) rot=(0,0.707107,0.707107;3.14159rad)
  sketch-geometry (1):
    g0: Circle CenterX=-14.4 CenterY=-21.9 CenterZ=0 NormalX=0 NormalY=0 NormalZ=1 AngleXU=0 Radius=0.9
  constraints (3):
    c: Diameter(g0) = 1.8
    c: DistanceX(g-3,g0) = 0
    c: DistanceY(g0,g-3) = 0.9
FEATURE [PartDesign::Pocket] Pocket124
  BaseFeature = -> Pocket123
  Direction = (0,-1,2e-16)
  Length = 3
  Length2 = 5
  Profile = -> Sketch335
  ReferenceAxis = -> Sketch335 [N_Axis]
  Refine = true
  Suppressed = false
  Type = 0
FEATURE [Sketcher::SketchObject] Sketch336
  ArcFitTolerance = 1e-06
  AttachmentSupport = -> [Pocket124]
  ExternalGeometry = -> [Pocket124]
  FullyConstrained = true
  MakeInternals = false
  MapMode = 5
  Placement = pos=(0,0,-1e-16) rot=(0,0,1;0rad)
  sketch-geometry (1):
    g0: Circle CenterX=11.75 CenterY=5.05 CenterZ=0 NormalX=0 NormalY=0 NormalZ=1 AngleXU=0 Radius=1.75
  constraints (3):
    c: Diameter(g0) = 3.5
    c: DistanceY(g0,g-4) = 6.05
    c: DistanceX(g-4,g0) = 11.75
FEATURE [PartDesign::Pad] Pad221
  BaseFeature = -> Pocket124
  Direction = (0,0,1)
  Length = 3.7
  Length2 = 10
  Profile = -> Sketch336
  ReferenceAxis = -> Sketch336 [N_Axis]
  Refine = true
  Suppressed = false
  Type = 0
FEATURE [Sketcher::SketchObject] Sketch337
  ArcFitTolerance = 1e-06
  AttachmentOffset = pos=(0,0,-0.75) rot=(0,0,1;0rad)
  AttachmentSupport = -> [Pad221]
  ExternalGeometry = -> [Pad221]
  FullyConstrained = true
  MakeInternals = false
  MapMode = 5
  Placement = pos=(0,13.35,-3.4e-15) rot=(0,0.707107,0.707107;3.14159rad)
  sketch-geometry (4):
    g0: LineSegment StartX=-11.4 StartY=-20.8 StartZ=0 EndX=-10.4 EndY=-20.8 EndZ=0
    g1: ArcOfCircle CenterX=-13.1 CenterY=-20.8 CenterZ=0 NormalX=0 NormalY=0 NormalZ=1 AngleXU=0 Radius=2.7 StartAngle=4.86222 EndAngle=6.28319
    g2: LineSegment StartX=-11.4 StartY=-20.8 StartZ=0 EndX=-11.4 EndY=-21 EndZ=0
    g3: ArcOfCircle CenterX=-14.4 CenterY=-21 CenterZ=0 NormalX=0 NormalY=0 NormalZ=1 AngleXU=0 Radius=2.99999 StartAngle=5.31607 EndAngle=6.28319
  constraints (13):
    c: PointOnObject(g0,g-4)
    c: Horizontal(g0)
    c: Coincident(g1,g0)
    c: PointOnObject(g1,g-3)
    c: DistanceY(g0,g-5) = 2.8
    c: DistanceX(g0,g0) = 1
    c: Radius(g1) = 2.7
    c: DistanceY(g1,g0) = 0
    c: Coincident(g2,g0)
    c: Coincident(g2,g-4)
    c: Coincident(g3,g2)
    c: Coincident(g3,g1)
    c: Tangent(g3,g-3)
FEATURE [PartDesign::Pad] Pad222
  BaseFeature = -> Pad221
  Direction = (0,1,-2e-16)
  Length = 2.5
  Length2 = 10
  Profile = -> Sketch337
  ReferenceAxis = -> Sketch337 [N_Axis]
  Refine = true
  Reversed = true
  Suppressed = false
  Type = 0
FEATURE [PartDesign::Fillet] Fillet014
  Base = -> Pad222 [Edge2,Edge1,Edge16,Edge81,Edge148,Edge90,Edge89,Edge75,Edge150,Edge80,Edge79,Edge88,Edge149,Edge77,Edge78,Edge87,Edge86,Edge61,Edge74]
  BaseFeature = -> Pad222
  Radius = 0.5
  Refine = true
  SupportTransform = false
  Suppressed = false
  UseAllEdges = false
FEATURE [PartDesign::Fillet] Fillet015
  Base = -> Fillet014 [Edge209]
  BaseFeature = -> Fillet014
  Radius = 0.25
  Refine = true
  SupportTransform = false
  Suppressed = false
  UseAllEdges = false
FEATURE [Sketcher::SketchObject] Sketch338
  ArcFitTolerance = 1e-06
  AttachmentSupport = -> [Fillet015]
  ExternalGeometry = -> [Fillet015]
  FullyConstrained = true
  MakeInternals = false
  MapMode = 5
  Placement = pos=(0,9.7,-2.2e-15) rot=(1,0,0;1.5708rad)
  sketch-geometry (4):
    g0: LineSegment StartX=16.95 StartY=-1.5 StartZ=0 EndX=16.95 EndY=-6.5 EndZ=0
    g1: LineSegment StartX=16.95 StartY=-6.5 StartZ=0 EndX=18.95 EndY=-6.5 EndZ=0
    g2: LineSegment StartX=18.95 StartY=-6.5 StartZ=0 EndX=18.95 EndY=-1.5 EndZ=0
    g3: LineSegment StartX=18.95 StartY=-1.5 StartZ=0 EndX=16.95 EndY=-1.5 EndZ=0
  constraints (11):
    c: Coincident(g0,g1)
    c: Coincident(g1,g2)
    c: Coincident(g2,g3)
    c: Coincident(g3,g0)
    c: Vertical(g0)
    c: Vertical(g2)
    c: Horizontal(g1)
    c: Horizontal(g3)
    c: PointOnObject(g1,g-4)
    c: Coincident(g-3,g0)
    c: DistanceY(g2,g2) = 5
FEATURE [PartDesign::Pad] Pad223
  BaseFeature = -> Fillet015
  Direction = (0,-1,2e-16)
  Length = 1
  Length2 = 10
  Profile = -> Sketch338
  ReferenceAxis = -> Sketch338 [N_Axis]
  Refine = true
  Suppressed = false
  Type = 0
FEATURE [PartDesign::Pad] Pad224
  BaseFeature = -> Pad223
  Direction = (0,-2e-16,-1)
  Length = 11.5
  Length2 = 10
  Profile = -> Pad223 [Face51]
  Refine = true
  Suppressed = false
  Type = 0
FEATURE [Sketcher::SketchObject] Sketch339
  ArcFitTolerance = 1e-06
  AttachmentSupport = -> [Pad224]
  ExternalGeometry = -> [Pad224]
  FullyConstrained = true
  MakeInternals = false
  MapMode = 5
  Placement = pos=(0,0,-18) rot=(1,0,0;3.14159rad)
  sketch-geometry (4):
    g0: LineSegment StartX=16.95 StartY=-3 StartZ=0 EndX=16.95 EndY=-3.1 EndZ=0
    g1: LineSegment StartX=16.95 StartY=-3.1 StartZ=0 EndX=18.95 EndY=-3.1 EndZ=0
    g2: LineSegment StartX=18.95 StartY=-3.1 StartZ=0 EndX=18.95 EndY=-3 EndZ=0
    g3: LineSegment StartX=18.95 StartY=-3 StartZ=0 EndX=16.95 EndY=-3 EndZ=0
  constraints (10):
    c: Coincident(g0,g1)
    c: Coincident(g1,g2)
    c: Coincident(g2,g3)
    c: Coincident(g3,g0)
    c: Vertical(g0)
    c: Vertical(g2)
    c: Horizontal(g1)
    c: Coincident(g0,g-3)
    c: DistanceY(g0,g0) = 0.1
    c: Coincident(g2,g-3)
FEATURE [PartDesign::Body] Body015  label="Pre_Right_Foot"
  AllowCompound = false
  Group = -> [Sketch319,Pad207,Sketch320,Pad208,Sketch321,Pad209,Sketch322,Pad210,Sketch323,Pad211,Sketch324,Pad212,Sketch325,Pad213,Sketch326,Pad214,Sketch327,Pad215,Sketch328,Pocket121,Sketch329,Pad216,Sketch330,Pad217,Pad218,Sketch331,Pocket122,Sketch332,Pad219,Sketch333,Pad220,Sketch334,Pocket123,Sketch335,Pocket124,Sketch336,Pad221,Sketch337,Pad222,Fillet014,Fillet015,Sketch338,Pad223,Pad224,Sketch339,+16 more]
  Origin = -> Origin015
  Placement = pos=(-67.75,1.4e-15,11.5) rot=(0,0,1;0rad)
  Tip = -> Pad246
